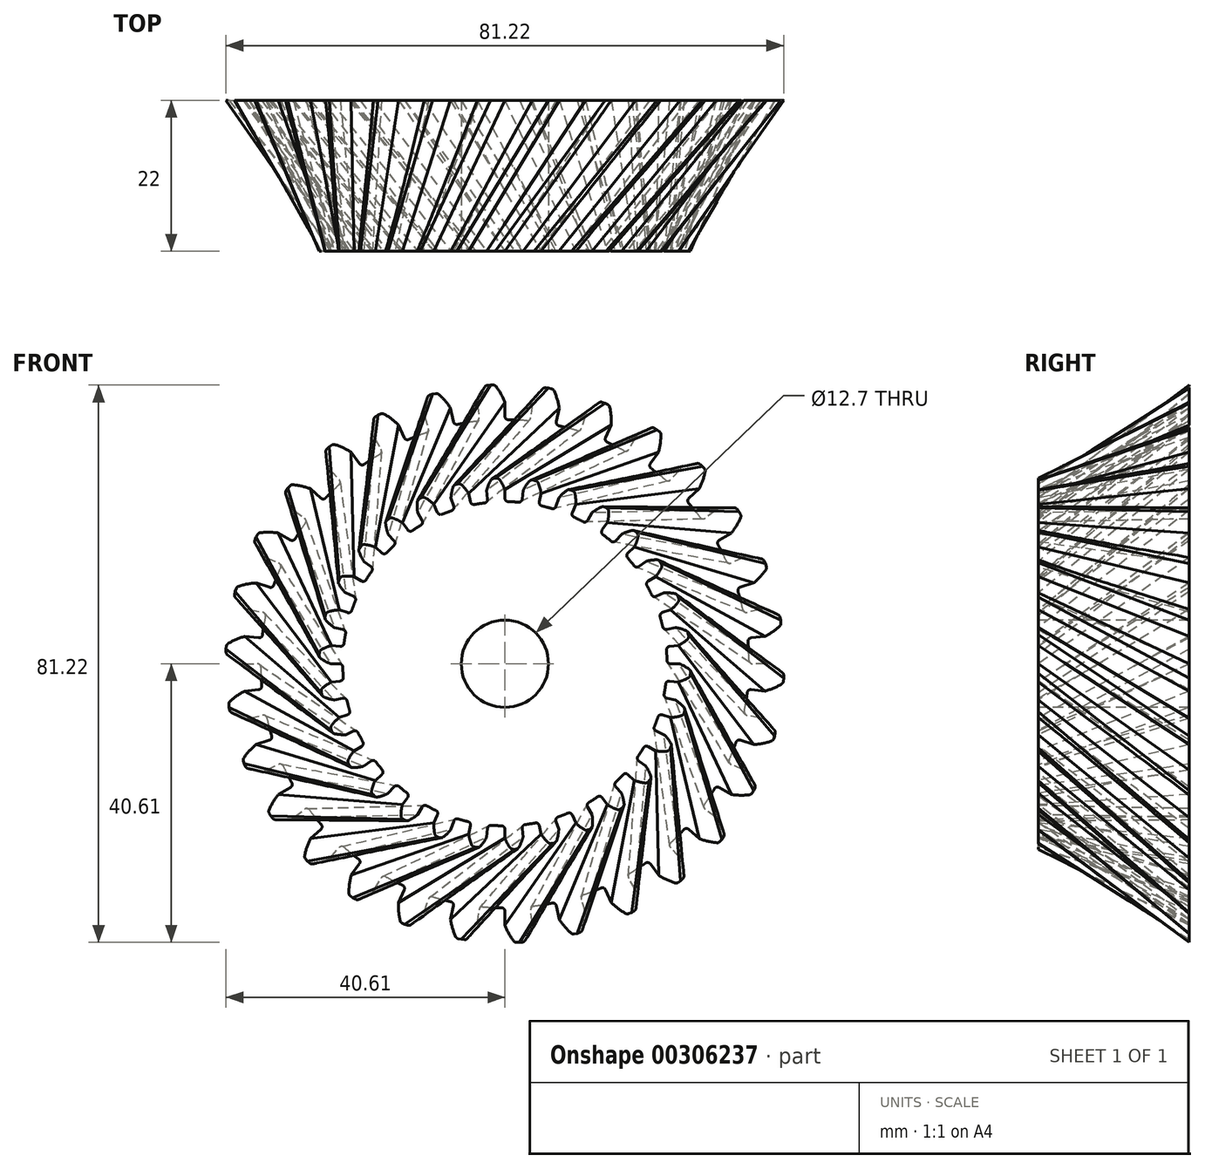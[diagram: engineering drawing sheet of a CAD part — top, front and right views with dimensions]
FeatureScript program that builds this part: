
annotation { "Feature Type Name" : "Feature", "Feature Type Description" : "" }
export const myFeature = defineFeature(function(context is Context, id is Id, definition is map)
    precondition{}
    {
        {
            var Q0;
            Q0=qCreatedBy(makeId("Front.planeOp"),FACE);
            var sketch = newSketch(context, id + "F0", { "sketchPlane" : qUnion([Q0])});
            skArc(sketch, "E0", {"start": v(-4.21, 35.3) * mm, "mid": v(-5.56, 35.12) * mm, "end": v(-6.9, 34.88) * mm});
            skLineSegment(sketch, "E1", {"start": v(0, 0) * mm, "end": v(-3.14, 59.92) * mm, "construction": true});
            skLineSegment(sketch, "E2", {"start": v(-1.69, 40.61) * mm, "end": v(-2.13, 40.61) * mm});
            skLineSegment(sketch, "E3", {"start": v(0, 38.1) * mm, "end": v(0, 36.06) * mm});
            skArc(sketch, "E4.trimOffspring", {"start": v(0, 38.1) * mm, "mid": v(-0.56, 39.3) * mm, "end": v(-1.28, 40.41) * mm});
            skLineSegment(sketch, "E5.MirrorCS", {"start": v(-2.57, 40.57) * mm, "end": v(-2.13, 40.61) * mm});
            skArc(sketch, "E6.MirrorCS", {"start": v(-3.98, 37.9) * mm, "mid": v(-3.55, 39.14) * mm, "end": v(-2.95, 40.32) * mm});
            skLineSegment(sketch, "E7.MirrorCS", {"start": v(-3.98, 37.9) * mm, "end": v(-3.77, 35.87) * mm});
            skPoint(sketch, "E8.visualSharp", {"position": v(-2.81, 40.54) * mm});
            skArc(sketch, "E8.filletArc", {"start": v(-2.57, 40.57) * mm, "mid": v(-2.79, 40.5) * mm, "end": v(-2.95, 40.32) * mm});
            skPoint(sketch, "E9.visualSharp", {"position": v(-1.44, 40.61) * mm});
            skArc(sketch, "E9.filletArc", {"start": v(-1.28, 40.41) * mm, "mid": v(-1.46, 40.56) * mm, "end": v(-1.69, 40.61) * mm});
            skPoint(sketch, "E10.orphan", {"position": v(-3.6, 34.32) * mm});
            skPoint(sketch, "E11.orphan", {"position": v(0, 34.5) * mm});
            skPoint(sketch, "E12.visualSharp", {"position": v(-3.72, 35.37) * mm});
            skArc(sketch, "E12.filletArc", {"start": v(-4.21, 35.3) * mm, "mid": v(-3.88, 35.5) * mm, "end": v(-3.77, 35.87) * mm});
            skPoint(sketch, "E13.visualSharp", {"position": v(0, 35.56) * mm});
            skArc(sketch, "E13.filletArc", {"start": v(0, 36.06) * mm, "mid": v(0.15, 35.7) * mm, "end": v(0.5, 35.56) * mm});
            skArc(sketch, "E14.1.0", {"start": v(-11.46, 33.66) * mm, "mid": v(-11.17, 33.91) * mm, "end": v(-11.14, 34.3) * mm});
            skLineSegment(sketch, "E14.1.1", {"start": v(-11.77, 36.24) * mm, "end": v(-11.14, 34.3) * mm});
            skArc(sketch, "E14.1.2", {"start": v(-11.77, 36.24) * mm, "mid": v(-11.61, 37.55) * mm, "end": v(-11.27, 38.83) * mm});
            skArc(sketch, "E14.1.3", {"start": v(-10.95, 39.15) * mm, "mid": v(-11.14, 39.03) * mm, "end": v(-11.27, 38.83) * mm});
            skLineSegment(sketch, "E14.1.4", {"start": v(-10.95, 39.15) * mm, "end": v(-10.53, 39.28) * mm});
            skLineSegment(sketch, "E14.1.5", {"start": v(-10.1, 39.38) * mm, "end": v(-10.53, 39.28) * mm});
            skArc(sketch, "E14.1.6", {"start": v(-9.66, 39.26) * mm, "mid": v(-9.86, 39.37) * mm, "end": v(-10.1, 39.38) * mm});
            skArc(sketch, "E14.1.7", {"start": v(-7.92, 37.27) * mm, "mid": v(-8.72, 38.33) * mm, "end": v(-9.66, 39.26) * mm});
            skLineSegment(sketch, "E14.1.8", {"start": v(-7.92, 37.27) * mm, "end": v(-7.5, 35.28) * mm});
            skArc(sketch, "E14.1.9", {"start": v(-7.5, 35.28) * mm, "mid": v(-7.28, 34.96) * mm, "end": v(-6.9, 34.88) * mm});
            skArc(sketch, "E14.2.0", {"start": v(-18.21, 30.54) * mm, "mid": v(-17.98, 30.85) * mm, "end": v(-18.03, 31.23) * mm});
            skLineSegment(sketch, "E14.2.1", {"start": v(-19.05, 33) * mm, "end": v(-18.03, 31.23) * mm});
            skArc(sketch, "E14.2.2", {"start": v(-19.05, 33) * mm, "mid": v(-19.16, 34.32) * mm, "end": v(-19.1, 35.64) * mm});
            skArc(sketch, "E14.2.3", {"start": v(-18.85, 36.02) * mm, "mid": v(-19.01, 35.86) * mm, "end": v(-19.1, 35.64) * mm});
            skLineSegment(sketch, "E14.2.4", {"start": v(-18.85, 36.02) * mm, "end": v(-18.46, 36.24) * mm});
            skLineSegment(sketch, "E14.2.5", {"start": v(-18.06, 36.42) * mm, "end": v(-18.46, 36.24) * mm});
            skArc(sketch, "E14.2.6", {"start": v(-17.6, 36.4) * mm, "mid": v(-17.83, 36.46) * mm, "end": v(-18.06, 36.42) * mm});
            skArc(sketch, "E14.2.7", {"start": v(-15.5, 34.8) * mm, "mid": v(-16.5, 35.68) * mm, "end": v(-17.6, 36.4) * mm});
            skLineSegment(sketch, "E14.2.8", {"start": v(-15.5, 34.8) * mm, "end": v(-14.67, 32.95) * mm});
            skArc(sketch, "E14.2.9", {"start": v(-14.67, 32.95) * mm, "mid": v(-14.4, 32.68) * mm, "end": v(-14, 32.69) * mm});
            skArc(sketch, "E14.3.0", {"start": v(-24.16, 26.09) * mm, "mid": v(-24, 26.44) * mm, "end": v(-24.13, 26.8) * mm});
            skLineSegment(sketch, "E14.3.1", {"start": v(-25.5, 28.31) * mm, "end": v(-24.13, 26.8) * mm});
            skArc(sketch, "E14.3.2", {"start": v(-25.5, 28.31) * mm, "mid": v(-25.88, 29.58) * mm, "end": v(-26.09, 30.9) * mm});
            skArc(sketch, "E14.3.3", {"start": v(-25.92, 31.31) * mm, "mid": v(-26.05, 31.12) * mm, "end": v(-26.09, 30.9) * mm});
            skLineSegment(sketch, "E14.3.4", {"start": v(-25.92, 31.31) * mm, "end": v(-25.6, 31.6) * mm});
            skLineSegment(sketch, "E14.3.5", {"start": v(-25.24, 31.87) * mm, "end": v(-25.6, 31.6) * mm});
            skArc(sketch, "E14.3.6", {"start": v(-24.8, 31.94) * mm, "mid": v(-25.02, 31.96) * mm, "end": v(-25.24, 31.87) * mm});
            skArc(sketch, "E14.3.7", {"start": v(-22.4, 30.82) * mm, "mid": v(-23.55, 31.47) * mm, "end": v(-24.8, 31.94) * mm});
            skLineSegment(sketch, "E14.3.8", {"start": v(-22.4, 30.82) * mm, "end": v(-21.2, 29.18) * mm});
            skArc(sketch, "E14.3.9", {"start": v(-21.2, 29.18) * mm, "mid": v(-20.87, 28.97) * mm, "end": v(-20.5, 29.06) * mm});
            skArc(sketch, "E14.4.0", {"start": v(-29.06, 20.5) * mm, "mid": v(-28.97, 20.87) * mm, "end": v(-29.18, 21.2) * mm});
            skLineSegment(sketch, "E14.4.1", {"start": v(-30.82, 22.4) * mm, "end": v(-29.18, 21.2) * mm});
            skArc(sketch, "E14.4.2", {"start": v(-30.82, 22.4) * mm, "mid": v(-31.47, 23.55) * mm, "end": v(-31.94, 24.8) * mm});
            skArc(sketch, "E14.4.3", {"start": v(-31.87, 25.24) * mm, "mid": v(-31.96, 25.02) * mm, "end": v(-31.94, 24.8) * mm});
            skLineSegment(sketch, "E14.4.4", {"start": v(-31.87, 25.24) * mm, "end": v(-31.6, 25.6) * mm});
            skLineSegment(sketch, "E14.4.5", {"start": v(-31.31, 25.92) * mm, "end": v(-31.6, 25.6) * mm});
            skArc(sketch, "E14.4.6", {"start": v(-30.9, 26.09) * mm, "mid": v(-31.12, 26.05) * mm, "end": v(-31.31, 25.92) * mm});
            skArc(sketch, "E14.4.7", {"start": v(-28.31, 25.5) * mm, "mid": v(-29.58, 25.88) * mm, "end": v(-30.9, 26.09) * mm});
            skLineSegment(sketch, "E14.4.8", {"start": v(-28.31, 25.5) * mm, "end": v(-26.8, 24.13) * mm});
            skArc(sketch, "E14.4.9", {"start": v(-26.8, 24.13) * mm, "mid": v(-26.44, 24) * mm, "end": v(-26.09, 24.16) * mm});
            skArc(sketch, "E14.5.0", {"start": v(-32.69, 14) * mm, "mid": v(-32.68, 14.4) * mm, "end": v(-32.95, 14.67) * mm});
            skLineSegment(sketch, "E14.5.1", {"start": v(-34.8, 15.5) * mm, "end": v(-32.95, 14.67) * mm});
            skArc(sketch, "E14.5.2", {"start": v(-34.8, 15.5) * mm, "mid": v(-35.68, 16.5) * mm, "end": v(-36.4, 17.6) * mm});
            skArc(sketch, "E14.5.3", {"start": v(-36.42, 18.06) * mm, "mid": v(-36.46, 17.83) * mm, "end": v(-36.4, 17.6) * mm});
            skLineSegment(sketch, "E14.5.4", {"start": v(-36.42, 18.06) * mm, "end": v(-36.24, 18.46) * mm});
            skLineSegment(sketch, "E14.5.5", {"start": v(-36.02, 18.85) * mm, "end": v(-36.24, 18.46) * mm});
            skArc(sketch, "E14.5.6", {"start": v(-35.64, 19.1) * mm, "mid": v(-35.86, 19.01) * mm, "end": v(-36.02, 18.85) * mm});
            skArc(sketch, "E14.5.7", {"start": v(-33, 19.05) * mm, "mid": v(-34.32, 19.16) * mm, "end": v(-35.64, 19.1) * mm});
            skLineSegment(sketch, "E14.5.8", {"start": v(-33, 19.05) * mm, "end": v(-31.23, 18.03) * mm});
            skArc(sketch, "E14.5.9", {"start": v(-31.23, 18.03) * mm, "mid": v(-30.85, 17.98) * mm, "end": v(-30.54, 18.21) * mm});
            skArc(sketch, "E14.6.0", {"start": v(-34.88, 6.9) * mm, "mid": v(-34.96, 7.28) * mm, "end": v(-35.28, 7.5) * mm});
            skLineSegment(sketch, "E14.6.1", {"start": v(-37.27, 7.92) * mm, "end": v(-35.28, 7.5) * mm});
            skArc(sketch, "E14.6.2", {"start": v(-37.27, 7.92) * mm, "mid": v(-38.33, 8.72) * mm, "end": v(-39.26, 9.66) * mm});
            skArc(sketch, "E14.6.3", {"start": v(-39.38, 10.1) * mm, "mid": v(-39.37, 9.86) * mm, "end": v(-39.26, 9.66) * mm});
            skLineSegment(sketch, "E14.6.4", {"start": v(-39.38, 10.1) * mm, "end": v(-39.28, 10.53) * mm});
            skLineSegment(sketch, "E14.6.5", {"start": v(-39.15, 10.95) * mm, "end": v(-39.28, 10.53) * mm});
            skArc(sketch, "E14.6.6", {"start": v(-38.83, 11.27) * mm, "mid": v(-39.03, 11.14) * mm, "end": v(-39.15, 10.95) * mm});
            skArc(sketch, "E14.6.7", {"start": v(-36.24, 11.77) * mm, "mid": v(-37.55, 11.61) * mm, "end": v(-38.83, 11.27) * mm});
            skLineSegment(sketch, "E14.6.8", {"start": v(-36.24, 11.77) * mm, "end": v(-34.3, 11.14) * mm});
            skArc(sketch, "E14.6.9", {"start": v(-34.3, 11.14) * mm, "mid": v(-33.91, 11.17) * mm, "end": v(-33.66, 11.46) * mm});
            skArc(sketch, "E14.7.0", {"start": v(-35.56, -0.5) * mm, "mid": v(-35.7, -0.15) * mm, "end": v(-36.06, 0) * mm});
            skLineSegment(sketch, "E14.7.1", {"start": v(-38.1, 0) * mm, "end": v(-36.06, 0) * mm});
            skArc(sketch, "E14.7.2", {"start": v(-38.1, 0) * mm, "mid": v(-39.3, 0.56) * mm, "end": v(-40.41, 1.28) * mm});
            skArc(sketch, "E14.7.3", {"start": v(-40.61, 1.69) * mm, "mid": v(-40.56, 1.46) * mm, "end": v(-40.41, 1.28) * mm});
            skLineSegment(sketch, "E14.7.4", {"start": v(-40.61, 1.69) * mm, "end": v(-40.61, 2.13) * mm});
            skLineSegment(sketch, "E14.7.5", {"start": v(-40.57, 2.57) * mm, "end": v(-40.61, 2.13) * mm});
            skArc(sketch, "E14.7.6", {"start": v(-40.32, 2.95) * mm, "mid": v(-40.5, 2.79) * mm, "end": v(-40.57, 2.57) * mm});
            skArc(sketch, "E14.7.7", {"start": v(-37.9, 3.98) * mm, "mid": v(-39.14, 3.55) * mm, "end": v(-40.32, 2.95) * mm});
            skLineSegment(sketch, "E14.7.8", {"start": v(-37.9, 3.98) * mm, "end": v(-35.87, 3.77) * mm});
            skArc(sketch, "E14.7.9", {"start": v(-35.87, 3.77) * mm, "mid": v(-35.5, 3.88) * mm, "end": v(-35.3, 4.21) * mm});
            skArc(sketch, "E14.8.0", {"start": v(-34.68, -7.88) * mm, "mid": v(-34.9, -7.57) * mm, "end": v(-35.28, -7.5) * mm});
            skLineSegment(sketch, "E14.8.1", {"start": v(-37.27, -7.92) * mm, "end": v(-35.28, -7.5) * mm});
            skArc(sketch, "E14.8.2", {"start": v(-37.27, -7.92) * mm, "mid": v(-38.56, -7.62) * mm, "end": v(-39.8, -7.15) * mm});
            skArc(sketch, "E14.8.3", {"start": v(-40.08, -6.8) * mm, "mid": v(-39.98, -7) * mm, "end": v(-39.8, -7.15) * mm});
            skLineSegment(sketch, "E14.8.4", {"start": v(-40.08, -6.8) * mm, "end": v(-40.17, -6.36) * mm});
            skLineSegment(sketch, "E14.8.5", {"start": v(-40.22, -5.92) * mm, "end": v(-40.17, -6.36) * mm});
            skArc(sketch, "E14.8.6", {"start": v(-40.06, -5.5) * mm, "mid": v(-40.19, -5.7) * mm, "end": v(-40.22, -5.92) * mm});
            skArc(sketch, "E14.8.7", {"start": v(-37.9, -3.98) * mm, "mid": v(-39.03, -4.67) * mm, "end": v(-40.06, -5.5) * mm});
            skLineSegment(sketch, "E14.8.8", {"start": v(-37.9, -3.98) * mm, "end": v(-35.87, -3.77) * mm});
            skArc(sketch, "E14.8.9", {"start": v(-35.87, -3.77) * mm, "mid": v(-35.53, -3.59) * mm, "end": v(-35.41, -3.22) * mm});
            skArc(sketch, "E14.9.0", {"start": v(-32.28, -14.92) * mm, "mid": v(-32.56, -14.66) * mm, "end": v(-32.95, -14.67) * mm});
            skLineSegment(sketch, "E14.9.1", {"start": v(-34.8, -15.5) * mm, "end": v(-32.95, -14.67) * mm});
            skArc(sketch, "E14.9.2", {"start": v(-34.8, -15.5) * mm, "mid": v(-36.13, -15.47) * mm, "end": v(-37.44, -15.27) * mm});
            skArc(sketch, "E14.9.3", {"start": v(-37.79, -14.98) * mm, "mid": v(-37.65, -15.16) * mm, "end": v(-37.44, -15.27) * mm});
            skLineSegment(sketch, "E14.9.4", {"start": v(-37.79, -14.98) * mm, "end": v(-37.97, -14.57) * mm});
            skLineSegment(sketch, "E14.9.5", {"start": v(-38.1, -14.16) * mm, "end": v(-37.97, -14.57) * mm});
            skArc(sketch, "E14.9.6", {"start": v(-38.04, -13.7) * mm, "mid": v(-38.12, -13.92) * mm, "end": v(-38.1, -14.16) * mm});
            skArc(sketch, "E14.9.7", {"start": v(-36.24, -11.77) * mm, "mid": v(-37.2, -12.68) * mm, "end": v(-38.04, -13.7) * mm});
            skLineSegment(sketch, "E14.9.8", {"start": v(-36.24, -11.77) * mm, "end": v(-34.3, -11.14) * mm});
            skArc(sketch, "E14.9.9", {"start": v(-34.3, -11.14) * mm, "mid": v(-34, -10.9) * mm, "end": v(-33.97, -10.51) * mm});
            skArc(sketch, "E14.10.0", {"start": v(-28.47, -21.3) * mm, "mid": v(-28.8, -21.1) * mm, "end": v(-29.18, -21.2) * mm});
            skLineSegment(sketch, "E14.10.1", {"start": v(-30.82, -22.4) * mm, "end": v(-29.18, -21.2) * mm});
            skArc(sketch, "E14.10.2", {"start": v(-30.82, -22.4) * mm, "mid": v(-32.12, -22.65) * mm, "end": v(-33.45, -22.72) * mm});
            skArc(sketch, "E14.10.3", {"start": v(-33.85, -22.5) * mm, "mid": v(-33.67, -22.66) * mm, "end": v(-33.45, -22.72) * mm});
            skLineSegment(sketch, "E14.10.4", {"start": v(-33.85, -22.5) * mm, "end": v(-34.1, -22.15) * mm});
            skLineSegment(sketch, "E14.10.5", {"start": v(-34.33, -21.77) * mm, "end": v(-34.1, -22.15) * mm});
            skArc(sketch, "E14.10.6", {"start": v(-34.36, -21.32) * mm, "mid": v(-34.4, -21.55) * mm, "end": v(-34.33, -21.77) * mm});
            skArc(sketch, "E14.10.7", {"start": v(-33, -19.05) * mm, "mid": v(-33.76, -20.14) * mm, "end": v(-34.36, -21.32) * mm});
            skLineSegment(sketch, "E14.10.8", {"start": v(-33, -19.05) * mm, "end": v(-31.23, -18.03) * mm});
            skArc(sketch, "E14.10.9", {"start": v(-31.23, -18.03) * mm, "mid": v(-31, -17.73) * mm, "end": v(-31.04, -17.34) * mm});
            skArc(sketch, "E14.11.0", {"start": v(-23.42, -26.76) * mm, "mid": v(-23.78, -26.63) * mm, "end": v(-24.13, -26.8) * mm});
            skLineSegment(sketch, "E14.11.1", {"start": v(-25.5, -28.31) * mm, "end": v(-24.13, -26.8) * mm});
            skArc(sketch, "E14.11.2", {"start": v(-25.5, -28.31) * mm, "mid": v(-26.71, -28.83) * mm, "end": v(-28, -29.17) * mm});
            skArc(sketch, "E14.11.3", {"start": v(-28.43, -29.05) * mm, "mid": v(-28.23, -29.16) * mm, "end": v(-28, -29.17) * mm});
            skLineSegment(sketch, "E14.11.4", {"start": v(-28.43, -29.05) * mm, "end": v(-28.76, -28.76) * mm});
            skLineSegment(sketch, "E14.11.5", {"start": v(-29.05, -28.43) * mm, "end": v(-28.76, -28.76) * mm});
            skArc(sketch, "E14.11.6", {"start": v(-29.17, -28) * mm, "mid": v(-29.16, -28.23) * mm, "end": v(-29.05, -28.43) * mm});
            skArc(sketch, "E14.11.7", {"start": v(-28.31, -25.5) * mm, "mid": v(-28.83, -26.71) * mm, "end": v(-29.17, -28) * mm});
            skLineSegment(sketch, "E14.11.8", {"start": v(-28.31, -25.5) * mm, "end": v(-26.8, -24.13) * mm});
            skArc(sketch, "E14.11.9", {"start": v(-26.8, -24.13) * mm, "mid": v(-26.63, -23.78) * mm, "end": v(-26.76, -23.42) * mm});
            skArc(sketch, "E14.12.0", {"start": v(-17.34, -31.04) * mm, "mid": v(-17.73, -31) * mm, "end": v(-18.03, -31.23) * mm});
            skLineSegment(sketch, "E14.12.1", {"start": v(-19.05, -33) * mm, "end": v(-18.03, -31.23) * mm});
            skArc(sketch, "E14.12.2", {"start": v(-19.05, -33) * mm, "mid": v(-20.14, -33.76) * mm, "end": v(-21.32, -34.36) * mm});
            skArc(sketch, "E14.12.3", {"start": v(-21.77, -34.33) * mm, "mid": v(-21.55, -34.4) * mm, "end": v(-21.32, -34.36) * mm});
            skLineSegment(sketch, "E14.12.4", {"start": v(-21.77, -34.33) * mm, "end": v(-22.15, -34.1) * mm});
            skLineSegment(sketch, "E14.12.5", {"start": v(-22.5, -33.85) * mm, "end": v(-22.15, -34.1) * mm});
            skArc(sketch, "E14.12.6", {"start": v(-22.72, -33.45) * mm, "mid": v(-22.66, -33.67) * mm, "end": v(-22.5, -33.85) * mm});
            skArc(sketch, "E14.12.7", {"start": v(-22.4, -30.82) * mm, "mid": v(-22.65, -32.12) * mm, "end": v(-22.72, -33.45) * mm});
            skLineSegment(sketch, "E14.12.8", {"start": v(-22.4, -30.82) * mm, "end": v(-21.2, -29.18) * mm});
            skArc(sketch, "E14.12.9", {"start": v(-21.2, -29.18) * mm, "mid": v(-21.1, -28.8) * mm, "end": v(-21.3, -28.47) * mm});
            skArc(sketch, "E14.13.0", {"start": v(-10.51, -33.97) * mm, "mid": v(-10.9, -34) * mm, "end": v(-11.14, -34.3) * mm});
            skLineSegment(sketch, "E14.13.1", {"start": v(-11.77, -36.24) * mm, "end": v(-11.14, -34.3) * mm});
            skArc(sketch, "E14.13.2", {"start": v(-11.77, -36.24) * mm, "mid": v(-12.68, -37.2) * mm, "end": v(-13.7, -38.04) * mm});
            skArc(sketch, "E14.13.3", {"start": v(-14.16, -38.1) * mm, "mid": v(-13.92, -38.12) * mm, "end": v(-13.7, -38.04) * mm});
            skLineSegment(sketch, "E14.13.4", {"start": v(-14.16, -38.1) * mm, "end": v(-14.57, -37.97) * mm});
            skLineSegment(sketch, "E14.13.5", {"start": v(-14.98, -37.79) * mm, "end": v(-14.57, -37.97) * mm});
            skArc(sketch, "E14.13.6", {"start": v(-15.27, -37.44) * mm, "mid": v(-15.16, -37.65) * mm, "end": v(-14.98, -37.79) * mm});
            skArc(sketch, "E14.13.7", {"start": v(-15.5, -34.8) * mm, "mid": v(-15.47, -36.13) * mm, "end": v(-15.27, -37.44) * mm});
            skLineSegment(sketch, "E14.13.8", {"start": v(-15.5, -34.8) * mm, "end": v(-14.67, -32.95) * mm});
            skArc(sketch, "E14.13.9", {"start": v(-14.67, -32.95) * mm, "mid": v(-14.66, -32.56) * mm, "end": v(-14.92, -32.28) * mm});
            skArc(sketch, "E14.14.0", {"start": v(-3.22, -35.41) * mm, "mid": v(-3.59, -35.53) * mm, "end": v(-3.77, -35.87) * mm});
            skLineSegment(sketch, "E14.14.1", {"start": v(-3.98, -37.9) * mm, "end": v(-3.77, -35.87) * mm});
            skArc(sketch, "E14.14.2", {"start": v(-3.98, -37.9) * mm, "mid": v(-4.67, -39.03) * mm, "end": v(-5.5, -40.06) * mm});
            skArc(sketch, "E14.14.3", {"start": v(-5.92, -40.22) * mm, "mid": v(-5.7, -40.19) * mm, "end": v(-5.5, -40.06) * mm});
            skLineSegment(sketch, "E14.14.4", {"start": v(-5.92, -40.22) * mm, "end": v(-6.36, -40.17) * mm});
            skLineSegment(sketch, "E14.14.5", {"start": v(-6.8, -40.08) * mm, "end": v(-6.36, -40.17) * mm});
            skArc(sketch, "E14.14.6", {"start": v(-7.15, -39.8) * mm, "mid": v(-7, -39.98) * mm, "end": v(-6.8, -40.08) * mm});
            skArc(sketch, "E14.14.7", {"start": v(-7.92, -37.27) * mm, "mid": v(-7.62, -38.56) * mm, "end": v(-7.15, -39.8) * mm});
            skLineSegment(sketch, "E14.14.8", {"start": v(-7.92, -37.27) * mm, "end": v(-7.5, -35.28) * mm});
            skArc(sketch, "E14.14.9", {"start": v(-7.5, -35.28) * mm, "mid": v(-7.57, -34.9) * mm, "end": v(-7.88, -34.68) * mm});
            skArc(sketch, "E14.15.0", {"start": v(4.21, -35.3) * mm, "mid": v(3.88, -35.5) * mm, "end": v(3.77, -35.87) * mm});
            skLineSegment(sketch, "E14.15.1", {"start": v(3.98, -37.9) * mm, "end": v(3.77, -35.87) * mm});
            skArc(sketch, "E14.15.2", {"start": v(3.98, -37.9) * mm, "mid": v(3.55, -39.14) * mm, "end": v(2.95, -40.32) * mm});
            skArc(sketch, "E14.15.3", {"start": v(2.57, -40.57) * mm, "mid": v(2.79, -40.5) * mm, "end": v(2.95, -40.32) * mm});
            skLineSegment(sketch, "E14.15.4", {"start": v(2.57, -40.57) * mm, "end": v(2.13, -40.61) * mm});
            skLineSegment(sketch, "E14.15.5", {"start": v(1.69, -40.61) * mm, "end": v(2.13, -40.61) * mm});
            skArc(sketch, "E14.15.6", {"start": v(1.28, -40.41) * mm, "mid": v(1.46, -40.56) * mm, "end": v(1.69, -40.61) * mm});
            skArc(sketch, "E14.15.7", {"start": v(0, -38.1) * mm, "mid": v(0.56, -39.3) * mm, "end": v(1.28, -40.41) * mm});
            skLineSegment(sketch, "E14.15.8", {"start": v(0, -38.1) * mm, "end": v(0, -36.06) * mm});
            skArc(sketch, "E14.15.9", {"start": v(0, -36.06) * mm, "mid": v(-0.15, -35.7) * mm, "end": v(-0.5, -35.56) * mm});
            skArc(sketch, "E14.16.0", {"start": v(11.46, -33.66) * mm, "mid": v(11.17, -33.91) * mm, "end": v(11.14, -34.3) * mm});
            skLineSegment(sketch, "E14.16.1", {"start": v(11.77, -36.24) * mm, "end": v(11.14, -34.3) * mm});
            skArc(sketch, "E14.16.2", {"start": v(11.77, -36.24) * mm, "mid": v(11.61, -37.55) * mm, "end": v(11.27, -38.83) * mm});
            skArc(sketch, "E14.16.3", {"start": v(10.95, -39.15) * mm, "mid": v(11.14, -39.03) * mm, "end": v(11.27, -38.83) * mm});
            skLineSegment(sketch, "E14.16.4", {"start": v(10.95, -39.15) * mm, "end": v(10.53, -39.28) * mm});
            skLineSegment(sketch, "E14.16.5", {"start": v(10.1, -39.38) * mm, "end": v(10.53, -39.28) * mm});
            skArc(sketch, "E14.16.6", {"start": v(9.66, -39.26) * mm, "mid": v(9.86, -39.37) * mm, "end": v(10.1, -39.38) * mm});
            skArc(sketch, "E14.16.7", {"start": v(7.92, -37.27) * mm, "mid": v(8.72, -38.33) * mm, "end": v(9.66, -39.26) * mm});
            skLineSegment(sketch, "E14.16.8", {"start": v(7.92, -37.27) * mm, "end": v(7.5, -35.28) * mm});
            skArc(sketch, "E14.16.9", {"start": v(7.5, -35.28) * mm, "mid": v(7.28, -34.96) * mm, "end": v(6.9, -34.88) * mm});
            skArc(sketch, "E14.17.0", {"start": v(18.21, -30.54) * mm, "mid": v(17.98, -30.85) * mm, "end": v(18.03, -31.23) * mm});
            skLineSegment(sketch, "E14.17.1", {"start": v(19.05, -33) * mm, "end": v(18.03, -31.23) * mm});
            skArc(sketch, "E14.17.2", {"start": v(19.05, -33) * mm, "mid": v(19.16, -34.32) * mm, "end": v(19.1, -35.64) * mm});
            skArc(sketch, "E14.17.3", {"start": v(18.85, -36.02) * mm, "mid": v(19.01, -35.86) * mm, "end": v(19.1, -35.64) * mm});
            skLineSegment(sketch, "E14.17.4", {"start": v(18.85, -36.02) * mm, "end": v(18.46, -36.24) * mm});
            skLineSegment(sketch, "E14.17.5", {"start": v(18.06, -36.42) * mm, "end": v(18.46, -36.24) * mm});
            skArc(sketch, "E14.17.6", {"start": v(17.6, -36.4) * mm, "mid": v(17.83, -36.46) * mm, "end": v(18.06, -36.42) * mm});
            skArc(sketch, "E14.17.7", {"start": v(15.5, -34.8) * mm, "mid": v(16.5, -35.68) * mm, "end": v(17.6, -36.4) * mm});
            skLineSegment(sketch, "E14.17.8", {"start": v(15.5, -34.8) * mm, "end": v(14.67, -32.95) * mm});
            skArc(sketch, "E14.17.9", {"start": v(14.67, -32.95) * mm, "mid": v(14.4, -32.68) * mm, "end": v(14, -32.69) * mm});
            skArc(sketch, "E14.18.0", {"start": v(24.16, -26.09) * mm, "mid": v(24, -26.44) * mm, "end": v(24.13, -26.8) * mm});
            skLineSegment(sketch, "E14.18.1", {"start": v(25.5, -28.31) * mm, "end": v(24.13, -26.8) * mm});
            skArc(sketch, "E14.18.2", {"start": v(25.5, -28.31) * mm, "mid": v(25.88, -29.58) * mm, "end": v(26.09, -30.9) * mm});
            skArc(sketch, "E14.18.3", {"start": v(25.92, -31.31) * mm, "mid": v(26.05, -31.12) * mm, "end": v(26.09, -30.9) * mm});
            skLineSegment(sketch, "E14.18.4", {"start": v(25.92, -31.31) * mm, "end": v(25.6, -31.6) * mm});
            skLineSegment(sketch, "E14.18.5", {"start": v(25.24, -31.87) * mm, "end": v(25.6, -31.6) * mm});
            skArc(sketch, "E14.18.6", {"start": v(24.8, -31.94) * mm, "mid": v(25.02, -31.96) * mm, "end": v(25.24, -31.87) * mm});
            skArc(sketch, "E14.18.7", {"start": v(22.4, -30.82) * mm, "mid": v(23.55, -31.47) * mm, "end": v(24.8, -31.94) * mm});
            skLineSegment(sketch, "E14.18.8", {"start": v(22.4, -30.82) * mm, "end": v(21.2, -29.18) * mm});
            skArc(sketch, "E14.18.9", {"start": v(21.2, -29.18) * mm, "mid": v(20.87, -28.97) * mm, "end": v(20.5, -29.06) * mm});
            skArc(sketch, "E14.19.0", {"start": v(29.06, -20.5) * mm, "mid": v(28.97, -20.87) * mm, "end": v(29.18, -21.2) * mm});
            skLineSegment(sketch, "E14.19.1", {"start": v(30.82, -22.4) * mm, "end": v(29.18, -21.2) * mm});
            skArc(sketch, "E14.19.2", {"start": v(30.82, -22.4) * mm, "mid": v(31.47, -23.55) * mm, "end": v(31.94, -24.8) * mm});
            skArc(sketch, "E14.19.3", {"start": v(31.87, -25.24) * mm, "mid": v(31.96, -25.02) * mm, "end": v(31.94, -24.8) * mm});
            skLineSegment(sketch, "E14.19.4", {"start": v(31.87, -25.24) * mm, "end": v(31.6, -25.6) * mm});
            skLineSegment(sketch, "E14.19.5", {"start": v(31.31, -25.92) * mm, "end": v(31.6, -25.6) * mm});
            skArc(sketch, "E14.19.6", {"start": v(30.9, -26.09) * mm, "mid": v(31.12, -26.05) * mm, "end": v(31.31, -25.92) * mm});
            skArc(sketch, "E14.19.7", {"start": v(28.31, -25.5) * mm, "mid": v(29.58, -25.88) * mm, "end": v(30.9, -26.09) * mm});
            skLineSegment(sketch, "E14.19.8", {"start": v(28.31, -25.5) * mm, "end": v(26.8, -24.13) * mm});
            skArc(sketch, "E14.19.9", {"start": v(26.8, -24.13) * mm, "mid": v(26.44, -24) * mm, "end": v(26.09, -24.16) * mm});
            skArc(sketch, "E14.20.0", {"start": v(32.69, -14) * mm, "mid": v(32.68, -14.4) * mm, "end": v(32.95, -14.67) * mm});
            skLineSegment(sketch, "E14.20.1", {"start": v(34.8, -15.5) * mm, "end": v(32.95, -14.67) * mm});
            skArc(sketch, "E14.20.2", {"start": v(34.8, -15.5) * mm, "mid": v(35.68, -16.5) * mm, "end": v(36.4, -17.6) * mm});
            skArc(sketch, "E14.20.3", {"start": v(36.42, -18.06) * mm, "mid": v(36.46, -17.83) * mm, "end": v(36.4, -17.6) * mm});
            skLineSegment(sketch, "E14.20.4", {"start": v(36.42, -18.06) * mm, "end": v(36.24, -18.46) * mm});
            skLineSegment(sketch, "E14.20.5", {"start": v(36.02, -18.85) * mm, "end": v(36.24, -18.46) * mm});
            skArc(sketch, "E14.20.6", {"start": v(35.64, -19.1) * mm, "mid": v(35.86, -19.01) * mm, "end": v(36.02, -18.85) * mm});
            skArc(sketch, "E14.20.7", {"start": v(33, -19.05) * mm, "mid": v(34.32, -19.16) * mm, "end": v(35.64, -19.1) * mm});
            skLineSegment(sketch, "E14.20.8", {"start": v(33, -19.05) * mm, "end": v(31.23, -18.03) * mm});
            skArc(sketch, "E14.20.9", {"start": v(31.23, -18.03) * mm, "mid": v(30.85, -17.98) * mm, "end": v(30.54, -18.21) * mm});
            skArc(sketch, "E14.21.0", {"start": v(34.88, -6.9) * mm, "mid": v(34.96, -7.28) * mm, "end": v(35.28, -7.5) * mm});
            skLineSegment(sketch, "E14.21.1", {"start": v(37.27, -7.92) * mm, "end": v(35.28, -7.5) * mm});
            skArc(sketch, "E14.21.2", {"start": v(37.27, -7.92) * mm, "mid": v(38.33, -8.72) * mm, "end": v(39.26, -9.66) * mm});
            skArc(sketch, "E14.21.3", {"start": v(39.38, -10.1) * mm, "mid": v(39.37, -9.86) * mm, "end": v(39.26, -9.66) * mm});
            skLineSegment(sketch, "E14.21.4", {"start": v(39.38, -10.1) * mm, "end": v(39.28, -10.53) * mm});
            skLineSegment(sketch, "E14.21.5", {"start": v(39.15, -10.95) * mm, "end": v(39.28, -10.53) * mm});
            skArc(sketch, "E14.21.6", {"start": v(38.83, -11.27) * mm, "mid": v(39.03, -11.14) * mm, "end": v(39.15, -10.95) * mm});
            skArc(sketch, "E14.21.7", {"start": v(36.24, -11.77) * mm, "mid": v(37.55, -11.61) * mm, "end": v(38.83, -11.27) * mm});
            skLineSegment(sketch, "E14.21.8", {"start": v(36.24, -11.77) * mm, "end": v(34.3, -11.14) * mm});
            skArc(sketch, "E14.21.9", {"start": v(34.3, -11.14) * mm, "mid": v(33.91, -11.17) * mm, "end": v(33.66, -11.46) * mm});
            skArc(sketch, "E14.22.0", {"start": v(35.56, 0.5) * mm, "mid": v(35.7, 0.15) * mm, "end": v(36.06, 0) * mm});
            skLineSegment(sketch, "E14.22.1", {"start": v(38.1, 0) * mm, "end": v(36.06, 0) * mm});
            skArc(sketch, "E14.22.2", {"start": v(38.1, 0) * mm, "mid": v(39.3, -0.56) * mm, "end": v(40.41, -1.28) * mm});
            skArc(sketch, "E14.22.3", {"start": v(40.61, -1.69) * mm, "mid": v(40.56, -1.46) * mm, "end": v(40.41, -1.28) * mm});
            skLineSegment(sketch, "E14.22.4", {"start": v(40.61, -1.69) * mm, "end": v(40.61, -2.13) * mm});
            skLineSegment(sketch, "E14.22.5", {"start": v(40.57, -2.57) * mm, "end": v(40.61, -2.13) * mm});
            skArc(sketch, "E14.22.6", {"start": v(40.32, -2.95) * mm, "mid": v(40.5, -2.79) * mm, "end": v(40.57, -2.57) * mm});
            skArc(sketch, "E14.22.7", {"start": v(37.9, -3.98) * mm, "mid": v(39.14, -3.55) * mm, "end": v(40.32, -2.95) * mm});
            skLineSegment(sketch, "E14.22.8", {"start": v(37.9, -3.98) * mm, "end": v(35.87, -3.77) * mm});
            skArc(sketch, "E14.22.9", {"start": v(35.87, -3.77) * mm, "mid": v(35.5, -3.88) * mm, "end": v(35.3, -4.21) * mm});
            skArc(sketch, "E14.23.0", {"start": v(34.68, 7.88) * mm, "mid": v(34.9, 7.57) * mm, "end": v(35.28, 7.5) * mm});
            skLineSegment(sketch, "E14.23.1", {"start": v(37.27, 7.92) * mm, "end": v(35.28, 7.5) * mm});
            skArc(sketch, "E14.23.2", {"start": v(37.27, 7.92) * mm, "mid": v(38.56, 7.62) * mm, "end": v(39.8, 7.15) * mm});
            skArc(sketch, "E14.23.3", {"start": v(40.08, 6.8) * mm, "mid": v(39.98, 7) * mm, "end": v(39.8, 7.15) * mm});
            skLineSegment(sketch, "E14.23.4", {"start": v(40.08, 6.8) * mm, "end": v(40.17, 6.36) * mm});
            skLineSegment(sketch, "E14.23.5", {"start": v(40.22, 5.92) * mm, "end": v(40.17, 6.36) * mm});
            skArc(sketch, "E14.23.6", {"start": v(40.06, 5.5) * mm, "mid": v(40.19, 5.7) * mm, "end": v(40.22, 5.92) * mm});
            skArc(sketch, "E14.23.7", {"start": v(37.9, 3.98) * mm, "mid": v(39.03, 4.67) * mm, "end": v(40.06, 5.5) * mm});
            skLineSegment(sketch, "E14.23.8", {"start": v(37.9, 3.98) * mm, "end": v(35.87, 3.77) * mm});
            skArc(sketch, "E14.23.9", {"start": v(35.87, 3.77) * mm, "mid": v(35.53, 3.59) * mm, "end": v(35.41, 3.22) * mm});
            skArc(sketch, "E14.24.0", {"start": v(32.28, 14.92) * mm, "mid": v(32.56, 14.66) * mm, "end": v(32.95, 14.67) * mm});
            skLineSegment(sketch, "E14.24.1", {"start": v(34.8, 15.5) * mm, "end": v(32.95, 14.67) * mm});
            skArc(sketch, "E14.24.2", {"start": v(34.8, 15.5) * mm, "mid": v(36.13, 15.47) * mm, "end": v(37.44, 15.27) * mm});
            skArc(sketch, "E14.24.3", {"start": v(37.79, 14.98) * mm, "mid": v(37.65, 15.16) * mm, "end": v(37.44, 15.27) * mm});
            skLineSegment(sketch, "E14.24.4", {"start": v(37.79, 14.98) * mm, "end": v(37.97, 14.57) * mm});
            skLineSegment(sketch, "E14.24.5", {"start": v(38.1, 14.16) * mm, "end": v(37.97, 14.57) * mm});
            skArc(sketch, "E14.24.6", {"start": v(38.04, 13.7) * mm, "mid": v(38.12, 13.92) * mm, "end": v(38.1, 14.16) * mm});
            skArc(sketch, "E14.24.7", {"start": v(36.24, 11.77) * mm, "mid": v(37.2, 12.68) * mm, "end": v(38.04, 13.7) * mm});
            skLineSegment(sketch, "E14.24.8", {"start": v(36.24, 11.77) * mm, "end": v(34.3, 11.14) * mm});
            skArc(sketch, "E14.24.9", {"start": v(34.3, 11.14) * mm, "mid": v(34, 10.9) * mm, "end": v(33.97, 10.51) * mm});
            skArc(sketch, "E14.25.0", {"start": v(28.47, 21.3) * mm, "mid": v(28.8, 21.1) * mm, "end": v(29.18, 21.2) * mm});
            skLineSegment(sketch, "E14.25.1", {"start": v(30.82, 22.4) * mm, "end": v(29.18, 21.2) * mm});
            skArc(sketch, "E14.25.2", {"start": v(30.82, 22.4) * mm, "mid": v(32.12, 22.65) * mm, "end": v(33.45, 22.72) * mm});
            skArc(sketch, "E14.25.3", {"start": v(33.85, 22.5) * mm, "mid": v(33.67, 22.66) * mm, "end": v(33.45, 22.72) * mm});
            skLineSegment(sketch, "E14.25.4", {"start": v(33.85, 22.5) * mm, "end": v(34.1, 22.15) * mm});
            skLineSegment(sketch, "E14.25.5", {"start": v(34.33, 21.77) * mm, "end": v(34.1, 22.15) * mm});
            skArc(sketch, "E14.25.6", {"start": v(34.36, 21.32) * mm, "mid": v(34.4, 21.55) * mm, "end": v(34.33, 21.77) * mm});
            skArc(sketch, "E14.25.7", {"start": v(33, 19.05) * mm, "mid": v(33.76, 20.14) * mm, "end": v(34.36, 21.32) * mm});
            skLineSegment(sketch, "E14.25.8", {"start": v(33, 19.05) * mm, "end": v(31.23, 18.03) * mm});
            skArc(sketch, "E14.25.9", {"start": v(31.23, 18.03) * mm, "mid": v(31, 17.73) * mm, "end": v(31.04, 17.34) * mm});
            skArc(sketch, "E14.26.0", {"start": v(23.42, 26.76) * mm, "mid": v(23.78, 26.63) * mm, "end": v(24.13, 26.8) * mm});
            skLineSegment(sketch, "E14.26.1", {"start": v(25.5, 28.31) * mm, "end": v(24.13, 26.8) * mm});
            skArc(sketch, "E14.26.2", {"start": v(25.5, 28.31) * mm, "mid": v(26.71, 28.83) * mm, "end": v(28, 29.17) * mm});
            skArc(sketch, "E14.26.3", {"start": v(28.43, 29.05) * mm, "mid": v(28.23, 29.16) * mm, "end": v(28, 29.17) * mm});
            skLineSegment(sketch, "E14.26.4", {"start": v(28.43, 29.05) * mm, "end": v(28.76, 28.76) * mm});
            skLineSegment(sketch, "E14.26.5", {"start": v(29.05, 28.43) * mm, "end": v(28.76, 28.76) * mm});
            skArc(sketch, "E14.26.6", {"start": v(29.17, 28) * mm, "mid": v(29.16, 28.23) * mm, "end": v(29.05, 28.43) * mm});
            skArc(sketch, "E14.26.7", {"start": v(28.31, 25.5) * mm, "mid": v(28.83, 26.71) * mm, "end": v(29.17, 28) * mm});
            skLineSegment(sketch, "E14.26.8", {"start": v(28.31, 25.5) * mm, "end": v(26.8, 24.13) * mm});
            skArc(sketch, "E14.26.9", {"start": v(26.8, 24.13) * mm, "mid": v(26.63, 23.78) * mm, "end": v(26.76, 23.42) * mm});
            skArc(sketch, "E14.27.0", {"start": v(17.34, 31.04) * mm, "mid": v(17.73, 31) * mm, "end": v(18.03, 31.23) * mm});
            skLineSegment(sketch, "E14.27.1", {"start": v(19.05, 33) * mm, "end": v(18.03, 31.23) * mm});
            skArc(sketch, "E14.27.2", {"start": v(19.05, 33) * mm, "mid": v(20.14, 33.76) * mm, "end": v(21.32, 34.36) * mm});
            skArc(sketch, "E14.27.3", {"start": v(21.77, 34.33) * mm, "mid": v(21.55, 34.4) * mm, "end": v(21.32, 34.36) * mm});
            skLineSegment(sketch, "E14.27.4", {"start": v(21.77, 34.33) * mm, "end": v(22.15, 34.1) * mm});
            skLineSegment(sketch, "E14.27.5", {"start": v(22.5, 33.85) * mm, "end": v(22.15, 34.1) * mm});
            skArc(sketch, "E14.27.6", {"start": v(22.72, 33.45) * mm, "mid": v(22.66, 33.67) * mm, "end": v(22.5, 33.85) * mm});
            skArc(sketch, "E14.27.7", {"start": v(22.4, 30.82) * mm, "mid": v(22.65, 32.12) * mm, "end": v(22.72, 33.45) * mm});
            skLineSegment(sketch, "E14.27.8", {"start": v(22.4, 30.82) * mm, "end": v(21.2, 29.18) * mm});
            skArc(sketch, "E14.27.9", {"start": v(21.2, 29.18) * mm, "mid": v(21.1, 28.8) * mm, "end": v(21.3, 28.47) * mm});
            skArc(sketch, "E14.28.0", {"start": v(10.51, 33.97) * mm, "mid": v(10.9, 34) * mm, "end": v(11.14, 34.3) * mm});
            skLineSegment(sketch, "E14.28.1", {"start": v(11.77, 36.24) * mm, "end": v(11.14, 34.3) * mm});
            skArc(sketch, "E14.28.2", {"start": v(11.77, 36.24) * mm, "mid": v(12.68, 37.2) * mm, "end": v(13.7, 38.04) * mm});
            skArc(sketch, "E14.28.3", {"start": v(14.16, 38.1) * mm, "mid": v(13.92, 38.12) * mm, "end": v(13.7, 38.04) * mm});
            skLineSegment(sketch, "E14.28.4", {"start": v(14.16, 38.1) * mm, "end": v(14.57, 37.97) * mm});
            skLineSegment(sketch, "E14.28.5", {"start": v(14.98, 37.79) * mm, "end": v(14.57, 37.97) * mm});
            skArc(sketch, "E14.28.6", {"start": v(15.27, 37.44) * mm, "mid": v(15.16, 37.65) * mm, "end": v(14.98, 37.79) * mm});
            skArc(sketch, "E14.28.7", {"start": v(15.5, 34.8) * mm, "mid": v(15.47, 36.13) * mm, "end": v(15.27, 37.44) * mm});
            skLineSegment(sketch, "E14.28.8", {"start": v(15.5, 34.8) * mm, "end": v(14.67, 32.95) * mm});
            skArc(sketch, "E14.28.9", {"start": v(14.67, 32.95) * mm, "mid": v(14.66, 32.56) * mm, "end": v(14.92, 32.28) * mm});
            skArc(sketch, "E14.29.0", {"start": v(3.22, 35.41) * mm, "mid": v(3.59, 35.53) * mm, "end": v(3.77, 35.87) * mm});
            skLineSegment(sketch, "E14.29.1", {"start": v(3.98, 37.9) * mm, "end": v(3.77, 35.87) * mm});
            skArc(sketch, "E14.29.2", {"start": v(3.98, 37.9) * mm, "mid": v(4.67, 39.03) * mm, "end": v(5.5, 40.06) * mm});
            skArc(sketch, "E14.29.3", {"start": v(5.92, 40.22) * mm, "mid": v(5.7, 40.19) * mm, "end": v(5.5, 40.06) * mm});
            skLineSegment(sketch, "E14.29.4", {"start": v(5.92, 40.22) * mm, "end": v(6.36, 40.17) * mm});
            skLineSegment(sketch, "E14.29.5", {"start": v(6.8, 40.08) * mm, "end": v(6.36, 40.17) * mm});
            skArc(sketch, "E14.29.6", {"start": v(7.15, 39.8) * mm, "mid": v(7, 39.98) * mm, "end": v(6.8, 40.08) * mm});
            skArc(sketch, "E14.29.7", {"start": v(7.92, 37.27) * mm, "mid": v(7.62, 38.56) * mm, "end": v(7.15, 39.8) * mm});
            skLineSegment(sketch, "E14.29.8", {"start": v(7.92, 37.27) * mm, "end": v(7.5, 35.28) * mm});
            skArc(sketch, "E14.29.9", {"start": v(7.5, 35.28) * mm, "mid": v(7.57, 34.9) * mm, "end": v(7.88, 34.68) * mm});
            skArc(sketch, "E15.trimOffspring", {"start": v(-11.46, 33.66) * mm, "mid": v(-12.74, 33.2) * mm, "end": v(-14, 32.69) * mm});
            skArc(sketch, "E16.trimOffspring", {"start": v(-18.21, 30.54) * mm, "mid": v(-19.37, 29.82) * mm, "end": v(-20.5, 29.06) * mm});
            skArc(sketch, "E17.trimOffspring", {"start": v(-24.16, 26.09) * mm, "mid": v(-25.14, 25.14) * mm, "end": v(-26.09, 24.16) * mm});
            skArc(sketch, "E18.trimOffspring", {"start": v(-29.06, 20.5) * mm, "mid": v(-29.82, 19.37) * mm, "end": v(-30.54, 18.21) * mm});
            skArc(sketch, "E19.trimOffspring", {"start": v(-32.69, 14) * mm, "mid": v(-33.2, 12.74) * mm, "end": v(-33.66, 11.46) * mm});
            skArc(sketch, "E20.trimOffspring", {"start": v(-34.88, 6.9) * mm, "mid": v(-35.12, 5.56) * mm, "end": v(-35.3, 4.21) * mm});
            skArc(sketch, "E21.trimOffspring", {"start": v(-35.56, -0.5) * mm, "mid": v(-35.51, -1.86) * mm, "end": v(-35.41, -3.22) * mm});
            skArc(sketch, "E22.trimOffspring", {"start": v(-34.68, -7.88) * mm, "mid": v(-34.35, -9.2) * mm, "end": v(-33.97, -10.51) * mm});
            skArc(sketch, "E23.trimOffspring", {"start": v(-32.28, -14.92) * mm, "mid": v(-31.68, -16.14) * mm, "end": v(-31.04, -17.34) * mm});
            skArc(sketch, "E24.trimOffspring", {"start": v(-28.47, -21.3) * mm, "mid": v(-27.64, -22.38) * mm, "end": v(-26.76, -23.42) * mm});
            skArc(sketch, "E25.trimOffspring", {"start": v(3.22, 35.41) * mm, "mid": v(1.86, 35.51) * mm, "end": v(0.5, 35.56) * mm});
            skArc(sketch, "E26.trimOffspring", {"start": v(10.51, 33.97) * mm, "mid": v(9.2, 34.35) * mm, "end": v(7.88, 34.68) * mm});
            skArc(sketch, "E27.trimOffspring", {"start": v(17.34, 31.04) * mm, "mid": v(16.14, 31.68) * mm, "end": v(14.92, 32.28) * mm});
            skArc(sketch, "E28.trimOffspring", {"start": v(23.42, 26.76) * mm, "mid": v(22.38, 27.64) * mm, "end": v(21.3, 28.47) * mm});
            skArc(sketch, "E29.trimOffspring", {"start": v(28.47, 21.3) * mm, "mid": v(27.64, 22.38) * mm, "end": v(26.76, 23.42) * mm});
            skArc(sketch, "E30.trimOffspring", {"start": v(32.28, 14.92) * mm, "mid": v(31.68, 16.14) * mm, "end": v(31.04, 17.34) * mm});
            skArc(sketch, "E31.trimOffspring", {"start": v(34.68, 7.88) * mm, "mid": v(34.35, 9.2) * mm, "end": v(33.97, 10.51) * mm});
            skArc(sketch, "E32.trimOffspring", {"start": v(35.56, 0.5) * mm, "mid": v(35.51, 1.86) * mm, "end": v(35.41, 3.22) * mm});
            skArc(sketch, "E33.trimOffspring", {"start": v(34.88, -6.9) * mm, "mid": v(35.12, -5.56) * mm, "end": v(35.3, -4.21) * mm});
            skArc(sketch, "E34.trimOffspring", {"start": v(32.69, -14) * mm, "mid": v(33.2, -12.74) * mm, "end": v(33.66, -11.46) * mm});
            skArc(sketch, "E35.trimOffspring", {"start": v(29.06, -20.5) * mm, "mid": v(29.82, -19.37) * mm, "end": v(30.54, -18.21) * mm});
            skArc(sketch, "E36.trimOffspring", {"start": v(24.16, -26.09) * mm, "mid": v(25.14, -25.14) * mm, "end": v(26.09, -24.16) * mm});
            skArc(sketch, "E37.trimOffspring", {"start": v(18.21, -30.54) * mm, "mid": v(19.37, -29.82) * mm, "end": v(20.5, -29.06) * mm});
            skArc(sketch, "E38.trimOffspring", {"start": v(11.46, -33.66) * mm, "mid": v(12.74, -33.2) * mm, "end": v(14, -32.69) * mm});
            skArc(sketch, "E39.trimOffspring", {"start": v(4.21, -35.3) * mm, "mid": v(5.56, -35.12) * mm, "end": v(6.9, -34.88) * mm});
            skArc(sketch, "E40.trimOffspring", {"start": v(-3.22, -35.41) * mm, "mid": v(-1.86, -35.51) * mm, "end": v(-0.5, -35.56) * mm});
            skArc(sketch, "E41.trimOffspring", {"start": v(-10.51, -33.97) * mm, "mid": v(-9.2, -34.35) * mm, "end": v(-7.88, -34.68) * mm});
            skArc(sketch, "E42.trimOffspring", {"start": v(-17.34, -31.04) * mm, "mid": v(-16.14, -31.68) * mm, "end": v(-14.92, -32.28) * mm});
            skArc(sketch, "E43.trimOffspring", {"start": v(-23.42, -26.76) * mm, "mid": v(-22.38, -27.64) * mm, "end": v(-21.3, -28.47) * mm});
            skSolve(sketch);
        }
        {
            var Q0;
            Q0=makeQuery(id+"F0.imprint","IMPRINT",FACE,{"disambiguationData":[TD([[makeQuery(id+"F0.imprint","IMPRINT",EDGE,{"derivedFrom":sQuery(id+"F0.wireOp",EDGE,"E0")}),1.0]])]});
            cPlane(context, id + "F1", {"entities" : qUnion([Q0]), "cplaneType" : CPlaneType.OFFSET, "offset" : 22 * mm, "width" : 152.4 * mm, "height" : 152.4 * mm});
        }
        {
            var Q0;
            Q0=qCreatedBy(id+"F1.planeOp",FACE);
            var sketch = newSketch(context, id + "F2", { "sketchPlane" : qUnion([Q0])});
            skArc(sketch, "E44", {"start": v(-2.96, 23.44) * mm, "mid": v(-3.7, 23.33) * mm, "end": v(-4.42, 23.2) * mm});
            skLineSegment(sketch, "E45", {"start": v(0, 0) * mm, "end": v(-2.34, 44.7) * mm, "construction": true});
            skLineSegment(sketch, "E46", {"start": v(-1.18, 27.04) * mm, "end": v(-1.42, 27.04) * mm});
            skLineSegment(sketch, "E47", {"start": v(0, 25.4) * mm, "end": v(0, 24.12) * mm});
            skArc(sketch, "E48.trimOffspring", {"start": v(0, 25.4) * mm, "mid": v(-0.34, 26.14) * mm, "end": v(-0.77, 26.82) * mm});
            skLineSegment(sketch, "E49.MirrorCS", {"start": v(-1.65, 27.01) * mm, "end": v(-1.42, 27.04) * mm});
            skArc(sketch, "E50.MirrorCS", {"start": v(-2.66, 25.26) * mm, "mid": v(-2.4, 26.03) * mm, "end": v(-2.04, 26.76) * mm});
            skLineSegment(sketch, "E51.MirrorCS", {"start": v(-2.66, 25.26) * mm, "end": v(-2.52, 24) * mm});
            skPoint(sketch, "E52.orphan", {"position": v(-2.08, 19.75) * mm});
            skPoint(sketch, "E53.orphan", {"position": v(0, 19.86) * mm});
            skPoint(sketch, "E54.visualSharp", {"position": v(-1.9, 26.98) * mm});
            skArc(sketch, "E54.filletArc", {"start": v(-1.65, 27.01) * mm, "mid": v(-1.88, 26.93) * mm, "end": v(-2.04, 26.76) * mm});
            skPoint(sketch, "E55.visualSharp", {"position": v(-0.93, 27.04) * mm});
            skArc(sketch, "E55.filletArc", {"start": v(-0.77, 26.82) * mm, "mid": v(-0.95, 26.98) * mm, "end": v(-1.18, 27.04) * mm});
            skPoint(sketch, "E56.visualSharp", {"position": v(0, 23.62) * mm});
            skArc(sketch, "E56.filletArc", {"start": v(0, 24.12) * mm, "mid": v(0.15, 23.77) * mm, "end": v(0.5, 23.62) * mm});
            skPoint(sketch, "E57.visualSharp", {"position": v(-2.47, 23.5) * mm});
            skArc(sketch, "E57.filletArc", {"start": v(-2.96, 23.44) * mm, "mid": v(-2.63, 23.62) * mm, "end": v(-2.52, 24) * mm});
            skArc(sketch, "E58.1.0", {"start": v(-7.77, 22.3) * mm, "mid": v(-7.48, 22.56) * mm, "end": v(-7.45, 22.94) * mm});
            skLineSegment(sketch, "E58.1.1", {"start": v(-7.85, 24.16) * mm, "end": v(-7.45, 22.94) * mm});
            skArc(sketch, "E58.1.2", {"start": v(-7.85, 24.16) * mm, "mid": v(-7.75, 24.96) * mm, "end": v(-7.56, 25.75) * mm});
            skArc(sketch, "E58.1.3", {"start": v(-7.23, 26.08) * mm, "mid": v(-7.43, 25.95) * mm, "end": v(-7.56, 25.75) * mm});
            skLineSegment(sketch, "E58.1.4", {"start": v(-7.23, 26.08) * mm, "end": v(-7, 26.15) * mm});
            skLineSegment(sketch, "E58.1.5", {"start": v(-6.78, 26.2) * mm, "end": v(-7, 26.15) * mm});
            skArc(sketch, "E58.1.6", {"start": v(-6.33, 26.08) * mm, "mid": v(-6.54, 26.2) * mm, "end": v(-6.78, 26.2) * mm});
            skArc(sketch, "E58.1.7", {"start": v(-5.28, 24.84) * mm, "mid": v(-5.77, 25.5) * mm, "end": v(-6.33, 26.08) * mm});
            skLineSegment(sketch, "E58.1.8", {"start": v(-5.28, 24.84) * mm, "end": v(-5.02, 23.6) * mm});
            skArc(sketch, "E58.1.9", {"start": v(-5.02, 23.6) * mm, "mid": v(-4.8, 23.28) * mm, "end": v(-4.42, 23.2) * mm});
            skArc(sketch, "E58.2.0", {"start": v(-12.24, 20.2) * mm, "mid": v(-12.01, 20.51) * mm, "end": v(-12.06, 20.9) * mm});
            skLineSegment(sketch, "E58.2.1", {"start": v(-12.7, 22) * mm, "end": v(-12.06, 20.9) * mm});
            skArc(sketch, "E58.2.2", {"start": v(-12.7, 22) * mm, "mid": v(-12.77, 22.8) * mm, "end": v(-12.75, 23.61) * mm});
            skArc(sketch, "E58.2.3", {"start": v(-12.5, 24) * mm, "mid": v(-12.67, 23.84) * mm, "end": v(-12.75, 23.61) * mm});
            skLineSegment(sketch, "E58.2.4", {"start": v(-12.5, 24) * mm, "end": v(-12.3, 24.12) * mm});
            skLineSegment(sketch, "E58.2.5", {"start": v(-12.07, 24.22) * mm, "end": v(-12.3, 24.12) * mm});
            skArc(sketch, "E58.2.6", {"start": v(-11.61, 24.2) * mm, "mid": v(-11.84, 24.26) * mm, "end": v(-12.07, 24.22) * mm});
            skArc(sketch, "E58.2.7", {"start": v(-10.33, 23.2) * mm, "mid": v(-10.94, 23.74) * mm, "end": v(-11.61, 24.2) * mm});
            skLineSegment(sketch, "E58.2.8", {"start": v(-10.33, 23.2) * mm, "end": v(-9.81, 22.04) * mm});
            skArc(sketch, "E58.2.9", {"start": v(-9.81, 22.04) * mm, "mid": v(-9.54, 21.77) * mm, "end": v(-9.15, 21.78) * mm});
            skArc(sketch, "E58.3.0", {"start": v(-16.17, 17.22) * mm, "mid": v(-16.01, 17.57) * mm, "end": v(-16.14, 17.93) * mm});
            skLineSegment(sketch, "E58.3.1", {"start": v(-17, 18.88) * mm, "end": v(-16.14, 17.93) * mm});
            skArc(sketch, "E58.3.2", {"start": v(-17, 18.88) * mm, "mid": v(-17.24, 19.65) * mm, "end": v(-17.38, 20.45) * mm});
            skArc(sketch, "E58.3.3", {"start": v(-17.21, 20.88) * mm, "mid": v(-17.35, 20.68) * mm, "end": v(-17.38, 20.45) * mm});
            skLineSegment(sketch, "E58.3.4", {"start": v(-17.21, 20.88) * mm, "end": v(-17.04, 21.04) * mm});
            skLineSegment(sketch, "E58.3.5", {"start": v(-16.85, 21.18) * mm, "end": v(-17.04, 21.04) * mm});
            skArc(sketch, "E58.3.6", {"start": v(-16.39, 21.25) * mm, "mid": v(-16.63, 21.27) * mm, "end": v(-16.85, 21.18) * mm});
            skArc(sketch, "E58.3.7", {"start": v(-14.93, 20.55) * mm, "mid": v(-15.64, 20.95) * mm, "end": v(-16.39, 21.25) * mm});
            skLineSegment(sketch, "E58.3.8", {"start": v(-14.93, 20.55) * mm, "end": v(-14.18, 19.52) * mm});
            skArc(sketch, "E58.3.9", {"start": v(-14.18, 19.52) * mm, "mid": v(-13.85, 19.31) * mm, "end": v(-13.48, 19.4) * mm});
            skArc(sketch, "E58.4.0", {"start": v(-19.4, 13.48) * mm, "mid": v(-19.31, 13.85) * mm, "end": v(-19.52, 14.18) * mm});
            skLineSegment(sketch, "E58.4.1", {"start": v(-20.55, 14.93) * mm, "end": v(-19.52, 14.18) * mm});
            skArc(sketch, "E58.4.2", {"start": v(-20.55, 14.93) * mm, "mid": v(-20.95, 15.64) * mm, "end": v(-21.25, 16.39) * mm});
            skArc(sketch, "E58.4.3", {"start": v(-21.18, 16.85) * mm, "mid": v(-21.27, 16.63) * mm, "end": v(-21.25, 16.39) * mm});
            skLineSegment(sketch, "E58.4.4", {"start": v(-21.18, 16.85) * mm, "end": v(-21.04, 17.04) * mm});
            skLineSegment(sketch, "E58.4.5", {"start": v(-20.88, 17.21) * mm, "end": v(-21.04, 17.04) * mm});
            skArc(sketch, "E58.4.6", {"start": v(-20.45, 17.38) * mm, "mid": v(-20.68, 17.35) * mm, "end": v(-20.88, 17.21) * mm});
            skArc(sketch, "E58.4.7", {"start": v(-18.88, 17) * mm, "mid": v(-19.65, 17.24) * mm, "end": v(-20.45, 17.38) * mm});
            skLineSegment(sketch, "E58.4.8", {"start": v(-18.88, 17) * mm, "end": v(-17.93, 16.14) * mm});
            skArc(sketch, "E58.4.9", {"start": v(-17.93, 16.14) * mm, "mid": v(-17.57, 16.01) * mm, "end": v(-17.22, 16.17) * mm});
            skArc(sketch, "E58.5.0", {"start": v(-21.78, 9.15) * mm, "mid": v(-21.77, 9.54) * mm, "end": v(-22.04, 9.81) * mm});
            skLineSegment(sketch, "E58.5.1", {"start": v(-23.2, 10.33) * mm, "end": v(-22.04, 9.81) * mm});
            skArc(sketch, "E58.5.2", {"start": v(-23.2, 10.33) * mm, "mid": v(-23.74, 10.94) * mm, "end": v(-24.2, 11.61) * mm});
            skArc(sketch, "E58.5.3", {"start": v(-24.22, 12.07) * mm, "mid": v(-24.26, 11.84) * mm, "end": v(-24.2, 11.61) * mm});
            skLineSegment(sketch, "E58.5.4", {"start": v(-24.22, 12.07) * mm, "end": v(-24.12, 12.3) * mm});
            skLineSegment(sketch, "E58.5.5", {"start": v(-24, 12.5) * mm, "end": v(-24.12, 12.3) * mm});
            skArc(sketch, "E58.5.6", {"start": v(-23.61, 12.75) * mm, "mid": v(-23.84, 12.67) * mm, "end": v(-24, 12.5) * mm});
            skArc(sketch, "E58.5.7", {"start": v(-22, 12.7) * mm, "mid": v(-22.8, 12.77) * mm, "end": v(-23.61, 12.75) * mm});
            skLineSegment(sketch, "E58.5.8", {"start": v(-22, 12.7) * mm, "end": v(-20.9, 12.06) * mm});
            skArc(sketch, "E58.5.9", {"start": v(-20.9, 12.06) * mm, "mid": v(-20.51, 12.01) * mm, "end": v(-20.2, 12.24) * mm});
            skArc(sketch, "E58.6.0", {"start": v(-23.2, 4.42) * mm, "mid": v(-23.28, 4.8) * mm, "end": v(-23.6, 5.02) * mm});
            skLineSegment(sketch, "E58.6.1", {"start": v(-24.84, 5.28) * mm, "end": v(-23.6, 5.02) * mm});
            skArc(sketch, "E58.6.2", {"start": v(-24.84, 5.28) * mm, "mid": v(-25.5, 5.77) * mm, "end": v(-26.08, 6.33) * mm});
            skArc(sketch, "E58.6.3", {"start": v(-26.2, 6.78) * mm, "mid": v(-26.2, 6.54) * mm, "end": v(-26.08, 6.33) * mm});
            skLineSegment(sketch, "E58.6.4", {"start": v(-26.2, 6.78) * mm, "end": v(-26.15, 7) * mm});
            skLineSegment(sketch, "E58.6.5", {"start": v(-26.08, 7.23) * mm, "end": v(-26.15, 7) * mm});
            skArc(sketch, "E58.6.6", {"start": v(-25.75, 7.56) * mm, "mid": v(-25.95, 7.43) * mm, "end": v(-26.08, 7.23) * mm});
            skArc(sketch, "E58.6.7", {"start": v(-24.16, 7.85) * mm, "mid": v(-24.96, 7.75) * mm, "end": v(-25.75, 7.56) * mm});
            skLineSegment(sketch, "E58.6.8", {"start": v(-24.16, 7.85) * mm, "end": v(-22.94, 7.45) * mm});
            skArc(sketch, "E58.6.9", {"start": v(-22.94, 7.45) * mm, "mid": v(-22.56, 7.48) * mm, "end": v(-22.3, 7.77) * mm});
            skArc(sketch, "E58.7.0", {"start": v(-23.62, -0.5) * mm, "mid": v(-23.77, -0.15) * mm, "end": v(-24.12, 0) * mm});
            skLineSegment(sketch, "E58.7.1", {"start": v(-25.4, 0) * mm, "end": v(-24.12, 0) * mm});
            skArc(sketch, "E58.7.2", {"start": v(-25.4, 0) * mm, "mid": v(-26.14, 0.34) * mm, "end": v(-26.82, 0.77) * mm});
            skArc(sketch, "E58.7.3", {"start": v(-27.04, 1.18) * mm, "mid": v(-26.98, 0.95) * mm, "end": v(-26.82, 0.77) * mm});
            skLineSegment(sketch, "E58.7.4", {"start": v(-27.04, 1.18) * mm, "end": v(-27.04, 1.42) * mm});
            skLineSegment(sketch, "E58.7.5", {"start": v(-27.01, 1.65) * mm, "end": v(-27.04, 1.42) * mm});
            skArc(sketch, "E58.7.6", {"start": v(-26.76, 2.04) * mm, "mid": v(-26.93, 1.88) * mm, "end": v(-27.01, 1.65) * mm});
            skArc(sketch, "E58.7.7", {"start": v(-25.26, 2.66) * mm, "mid": v(-26.03, 2.4) * mm, "end": v(-26.76, 2.04) * mm});
            skLineSegment(sketch, "E58.7.8", {"start": v(-25.26, 2.66) * mm, "end": v(-24, 2.52) * mm});
            skArc(sketch, "E58.7.9", {"start": v(-24, 2.52) * mm, "mid": v(-23.62, 2.63) * mm, "end": v(-23.44, 2.96) * mm});
            skArc(sketch, "E58.8.0", {"start": v(-23, -5.4) * mm, "mid": v(-23.22, -5.08) * mm, "end": v(-23.6, -5.02) * mm});
            skLineSegment(sketch, "E58.8.1", {"start": v(-24.84, -5.28) * mm, "end": v(-23.6, -5.02) * mm});
            skArc(sketch, "E58.8.2", {"start": v(-24.84, -5.28) * mm, "mid": v(-25.64, -5.1) * mm, "end": v(-26.4, -4.83) * mm});
            skArc(sketch, "E58.8.3", {"start": v(-26.69, -4.47) * mm, "mid": v(-26.59, -4.68) * mm, "end": v(-26.4, -4.83) * mm});
            skLineSegment(sketch, "E58.8.4", {"start": v(-26.69, -4.47) * mm, "end": v(-26.74, -4.24) * mm});
            skLineSegment(sketch, "E58.8.5", {"start": v(-26.76, -4) * mm, "end": v(-26.74, -4.24) * mm});
            skArc(sketch, "E58.8.6", {"start": v(-26.6, -3.57) * mm, "mid": v(-26.73, -3.76) * mm, "end": v(-26.76, -4) * mm});
            skArc(sketch, "E58.8.7", {"start": v(-25.26, -2.66) * mm, "mid": v(-25.96, -3.07) * mm, "end": v(-26.6, -3.57) * mm});
            skLineSegment(sketch, "E58.8.8", {"start": v(-25.26, -2.66) * mm, "end": v(-24, -2.52) * mm});
            skArc(sketch, "E58.8.9", {"start": v(-24, -2.52) * mm, "mid": v(-23.65, -2.34) * mm, "end": v(-23.54, -1.97) * mm});
            skArc(sketch, "E58.9.0", {"start": v(-21.37, -10.06) * mm, "mid": v(-21.66, -9.8) * mm, "end": v(-22.04, -9.81) * mm});
            skLineSegment(sketch, "E58.9.1", {"start": v(-23.2, -10.33) * mm, "end": v(-22.04, -9.81) * mm});
            skArc(sketch, "E58.9.2", {"start": v(-23.2, -10.33) * mm, "mid": v(-24.01, -10.32) * mm, "end": v(-24.82, -10.2) * mm});
            skArc(sketch, "E58.9.3", {"start": v(-25.18, -9.92) * mm, "mid": v(-25.03, -10.1) * mm, "end": v(-24.82, -10.2) * mm});
            skLineSegment(sketch, "E58.9.4", {"start": v(-25.18, -9.92) * mm, "end": v(-25.27, -9.7) * mm});
            skLineSegment(sketch, "E58.9.5", {"start": v(-25.35, -9.48) * mm, "end": v(-25.27, -9.7) * mm});
            skArc(sketch, "E58.9.6", {"start": v(-25.27, -9.02) * mm, "mid": v(-25.37, -9.24) * mm, "end": v(-25.35, -9.48) * mm});
            skArc(sketch, "E58.9.7", {"start": v(-24.16, -7.85) * mm, "mid": v(-24.75, -8.4) * mm, "end": v(-25.27, -9.02) * mm});
            skLineSegment(sketch, "E58.9.8", {"start": v(-24.16, -7.85) * mm, "end": v(-22.94, -7.45) * mm});
            skArc(sketch, "E58.9.9", {"start": v(-22.94, -7.45) * mm, "mid": v(-22.65, -7.2) * mm, "end": v(-22.61, -6.83) * mm});
            skArc(sketch, "E58.10.0", {"start": v(-18.81, -14.28) * mm, "mid": v(-19.14, -14.09) * mm, "end": v(-19.52, -14.18) * mm});
            skLineSegment(sketch, "E58.10.1", {"start": v(-20.55, -14.93) * mm, "end": v(-19.52, -14.18) * mm});
            skArc(sketch, "E58.10.2", {"start": v(-20.55, -14.93) * mm, "mid": v(-21.34, -15.09) * mm, "end": v(-22.15, -15.14) * mm});
            skArc(sketch, "E58.10.3", {"start": v(-22.57, -14.94) * mm, "mid": v(-22.38, -15.1) * mm, "end": v(-22.15, -15.14) * mm});
            skLineSegment(sketch, "E58.10.4", {"start": v(-22.57, -14.94) * mm, "end": v(-22.7, -14.74) * mm});
            skLineSegment(sketch, "E58.10.5", {"start": v(-22.82, -14.54) * mm, "end": v(-22.7, -14.74) * mm});
            skArc(sketch, "E58.10.6", {"start": v(-22.85, -14.08) * mm, "mid": v(-22.9, -14.31) * mm, "end": v(-22.82, -14.54) * mm});
            skArc(sketch, "E58.10.7", {"start": v(-22, -12.7) * mm, "mid": v(-22.47, -13.36) * mm, "end": v(-22.85, -14.08) * mm});
            skLineSegment(sketch, "E58.10.8", {"start": v(-22, -12.7) * mm, "end": v(-20.9, -12.06) * mm});
            skArc(sketch, "E58.10.9", {"start": v(-20.9, -12.06) * mm, "mid": v(-20.66, -11.76) * mm, "end": v(-20.7, -11.38) * mm});
            skArc(sketch, "E58.11.0", {"start": v(-15.43, -17.88) * mm, "mid": v(-15.8, -17.76) * mm, "end": v(-16.14, -17.93) * mm});
            skLineSegment(sketch, "E58.11.1", {"start": v(-17, -18.88) * mm, "end": v(-16.14, -17.93) * mm});
            skArc(sketch, "E58.11.2", {"start": v(-17, -18.88) * mm, "mid": v(-17.74, -19.2) * mm, "end": v(-18.52, -19.42) * mm});
            skArc(sketch, "E58.11.3", {"start": v(-18.97, -19.3) * mm, "mid": v(-18.76, -19.41) * mm, "end": v(-18.52, -19.42) * mm});
            skLineSegment(sketch, "E58.11.4", {"start": v(-18.97, -19.3) * mm, "end": v(-19.14, -19.14) * mm});
            skLineSegment(sketch, "E58.11.5", {"start": v(-19.3, -18.97) * mm, "end": v(-19.14, -19.14) * mm});
            skArc(sketch, "E58.11.6", {"start": v(-19.42, -18.52) * mm, "mid": v(-19.41, -18.76) * mm, "end": v(-19.3, -18.97) * mm});
            skArc(sketch, "E58.11.7", {"start": v(-18.88, -17) * mm, "mid": v(-19.2, -17.74) * mm, "end": v(-19.42, -18.52) * mm});
            skLineSegment(sketch, "E58.11.8", {"start": v(-18.88, -17) * mm, "end": v(-17.93, -16.14) * mm});
            skArc(sketch, "E58.11.9", {"start": v(-17.93, -16.14) * mm, "mid": v(-17.76, -15.8) * mm, "end": v(-17.88, -15.43) * mm});
            skArc(sketch, "E58.12.0", {"start": v(-11.38, -20.7) * mm, "mid": v(-11.76, -20.66) * mm, "end": v(-12.06, -20.9) * mm});
            skLineSegment(sketch, "E58.12.1", {"start": v(-12.7, -22) * mm, "end": v(-12.06, -20.9) * mm});
            skArc(sketch, "E58.12.2", {"start": v(-12.7, -22) * mm, "mid": v(-13.36, -22.47) * mm, "end": v(-14.08, -22.85) * mm});
            skArc(sketch, "E58.12.3", {"start": v(-14.54, -22.82) * mm, "mid": v(-14.31, -22.9) * mm, "end": v(-14.08, -22.85) * mm});
            skLineSegment(sketch, "E58.12.4", {"start": v(-14.54, -22.82) * mm, "end": v(-14.74, -22.7) * mm});
            skLineSegment(sketch, "E58.12.5", {"start": v(-14.94, -22.57) * mm, "end": v(-14.74, -22.7) * mm});
            skArc(sketch, "E58.12.6", {"start": v(-15.14, -22.15) * mm, "mid": v(-15.1, -22.38) * mm, "end": v(-14.94, -22.57) * mm});
            skArc(sketch, "E58.12.7", {"start": v(-14.93, -20.55) * mm, "mid": v(-15.09, -21.34) * mm, "end": v(-15.14, -22.15) * mm});
            skLineSegment(sketch, "E58.12.8", {"start": v(-14.93, -20.55) * mm, "end": v(-14.18, -19.52) * mm});
            skArc(sketch, "E58.12.9", {"start": v(-14.18, -19.52) * mm, "mid": v(-14.09, -19.14) * mm, "end": v(-14.28, -18.81) * mm});
            skArc(sketch, "E58.13.0", {"start": v(-6.83, -22.61) * mm, "mid": v(-7.2, -22.65) * mm, "end": v(-7.45, -22.94) * mm});
            skLineSegment(sketch, "E58.13.1", {"start": v(-7.85, -24.16) * mm, "end": v(-7.45, -22.94) * mm});
            skArc(sketch, "E58.13.2", {"start": v(-7.85, -24.16) * mm, "mid": v(-8.4, -24.75) * mm, "end": v(-9.02, -25.27) * mm});
            skArc(sketch, "E58.13.3", {"start": v(-9.48, -25.35) * mm, "mid": v(-9.24, -25.37) * mm, "end": v(-9.02, -25.27) * mm});
            skLineSegment(sketch, "E58.13.4", {"start": v(-9.48, -25.35) * mm, "end": v(-9.7, -25.27) * mm});
            skLineSegment(sketch, "E58.13.5", {"start": v(-9.92, -25.18) * mm, "end": v(-9.7, -25.27) * mm});
            skArc(sketch, "E58.13.6", {"start": v(-10.2, -24.82) * mm, "mid": v(-10.1, -25.03) * mm, "end": v(-9.92, -25.18) * mm});
            skArc(sketch, "E58.13.7", {"start": v(-10.33, -23.2) * mm, "mid": v(-10.32, -24.01) * mm, "end": v(-10.2, -24.82) * mm});
            skLineSegment(sketch, "E58.13.8", {"start": v(-10.33, -23.2) * mm, "end": v(-9.81, -22.04) * mm});
            skArc(sketch, "E58.13.9", {"start": v(-9.81, -22.04) * mm, "mid": v(-9.8, -21.66) * mm, "end": v(-10.06, -21.37) * mm});
            skArc(sketch, "E58.14.0", {"start": v(-1.97, -23.54) * mm, "mid": v(-2.34, -23.65) * mm, "end": v(-2.52, -24) * mm});
            skLineSegment(sketch, "E58.14.1", {"start": v(-2.66, -25.26) * mm, "end": v(-2.52, -24) * mm});
            skArc(sketch, "E58.14.2", {"start": v(-2.66, -25.26) * mm, "mid": v(-3.07, -25.96) * mm, "end": v(-3.57, -26.6) * mm});
            skArc(sketch, "E58.14.3", {"start": v(-4, -26.76) * mm, "mid": v(-3.76, -26.73) * mm, "end": v(-3.57, -26.6) * mm});
            skLineSegment(sketch, "E58.14.4", {"start": v(-4, -26.76) * mm, "end": v(-4.24, -26.74) * mm});
            skLineSegment(sketch, "E58.14.5", {"start": v(-4.47, -26.69) * mm, "end": v(-4.24, -26.74) * mm});
            skArc(sketch, "E58.14.6", {"start": v(-4.83, -26.4) * mm, "mid": v(-4.68, -26.59) * mm, "end": v(-4.47, -26.69) * mm});
            skArc(sketch, "E58.14.7", {"start": v(-5.28, -24.84) * mm, "mid": v(-5.1, -25.64) * mm, "end": v(-4.83, -26.4) * mm});
            skLineSegment(sketch, "E58.14.8", {"start": v(-5.28, -24.84) * mm, "end": v(-5.02, -23.6) * mm});
            skArc(sketch, "E58.14.9", {"start": v(-5.02, -23.6) * mm, "mid": v(-5.08, -23.22) * mm, "end": v(-5.4, -23) * mm});
            skArc(sketch, "E58.15.0", {"start": v(2.96, -23.44) * mm, "mid": v(2.63, -23.62) * mm, "end": v(2.52, -24) * mm});
            skLineSegment(sketch, "E58.15.1", {"start": v(2.66, -25.26) * mm, "end": v(2.52, -24) * mm});
            skArc(sketch, "E58.15.2", {"start": v(2.66, -25.26) * mm, "mid": v(2.4, -26.03) * mm, "end": v(2.04, -26.76) * mm});
            skArc(sketch, "E58.15.3", {"start": v(1.65, -27.01) * mm, "mid": v(1.88, -26.93) * mm, "end": v(2.04, -26.76) * mm});
            skLineSegment(sketch, "E58.15.4", {"start": v(1.65, -27.01) * mm, "end": v(1.42, -27.04) * mm});
            skLineSegment(sketch, "E58.15.5", {"start": v(1.18, -27.04) * mm, "end": v(1.42, -27.04) * mm});
            skArc(sketch, "E58.15.6", {"start": v(0.77, -26.82) * mm, "mid": v(0.95, -26.98) * mm, "end": v(1.18, -27.04) * mm});
            skArc(sketch, "E58.15.7", {"start": v(0, -25.4) * mm, "mid": v(0.34, -26.14) * mm, "end": v(0.77, -26.82) * mm});
            skLineSegment(sketch, "E58.15.8", {"start": v(0, -25.4) * mm, "end": v(0, -24.12) * mm});
            skArc(sketch, "E58.15.9", {"start": v(0, -24.12) * mm, "mid": v(-0.15, -23.77) * mm, "end": v(-0.5, -23.62) * mm});
            skArc(sketch, "E58.16.0", {"start": v(7.77, -22.3) * mm, "mid": v(7.48, -22.56) * mm, "end": v(7.45, -22.94) * mm});
            skLineSegment(sketch, "E58.16.1", {"start": v(7.85, -24.16) * mm, "end": v(7.45, -22.94) * mm});
            skArc(sketch, "E58.16.2", {"start": v(7.85, -24.16) * mm, "mid": v(7.75, -24.96) * mm, "end": v(7.56, -25.75) * mm});
            skArc(sketch, "E58.16.3", {"start": v(7.23, -26.08) * mm, "mid": v(7.43, -25.95) * mm, "end": v(7.56, -25.75) * mm});
            skLineSegment(sketch, "E58.16.4", {"start": v(7.23, -26.08) * mm, "end": v(7, -26.15) * mm});
            skLineSegment(sketch, "E58.16.5", {"start": v(6.78, -26.2) * mm, "end": v(7, -26.15) * mm});
            skArc(sketch, "E58.16.6", {"start": v(6.33, -26.08) * mm, "mid": v(6.54, -26.2) * mm, "end": v(6.78, -26.2) * mm});
            skArc(sketch, "E58.16.7", {"start": v(5.28, -24.84) * mm, "mid": v(5.77, -25.5) * mm, "end": v(6.33, -26.08) * mm});
            skLineSegment(sketch, "E58.16.8", {"start": v(5.28, -24.84) * mm, "end": v(5.02, -23.6) * mm});
            skArc(sketch, "E58.16.9", {"start": v(5.02, -23.6) * mm, "mid": v(4.8, -23.28) * mm, "end": v(4.42, -23.2) * mm});
            skArc(sketch, "E58.17.0", {"start": v(12.24, -20.2) * mm, "mid": v(12.01, -20.51) * mm, "end": v(12.06, -20.9) * mm});
            skLineSegment(sketch, "E58.17.1", {"start": v(12.7, -22) * mm, "end": v(12.06, -20.9) * mm});
            skArc(sketch, "E58.17.2", {"start": v(12.7, -22) * mm, "mid": v(12.77, -22.8) * mm, "end": v(12.75, -23.61) * mm});
            skArc(sketch, "E58.17.3", {"start": v(12.5, -24) * mm, "mid": v(12.67, -23.84) * mm, "end": v(12.75, -23.61) * mm});
            skLineSegment(sketch, "E58.17.4", {"start": v(12.5, -24) * mm, "end": v(12.3, -24.12) * mm});
            skLineSegment(sketch, "E58.17.5", {"start": v(12.07, -24.22) * mm, "end": v(12.3, -24.12) * mm});
            skArc(sketch, "E58.17.6", {"start": v(11.61, -24.2) * mm, "mid": v(11.84, -24.26) * mm, "end": v(12.07, -24.22) * mm});
            skArc(sketch, "E58.17.7", {"start": v(10.33, -23.2) * mm, "mid": v(10.94, -23.74) * mm, "end": v(11.61, -24.2) * mm});
            skLineSegment(sketch, "E58.17.8", {"start": v(10.33, -23.2) * mm, "end": v(9.81, -22.04) * mm});
            skArc(sketch, "E58.17.9", {"start": v(9.81, -22.04) * mm, "mid": v(9.54, -21.77) * mm, "end": v(9.15, -21.78) * mm});
            skArc(sketch, "E58.18.0", {"start": v(16.17, -17.22) * mm, "mid": v(16.01, -17.57) * mm, "end": v(16.14, -17.93) * mm});
            skLineSegment(sketch, "E58.18.1", {"start": v(17, -18.88) * mm, "end": v(16.14, -17.93) * mm});
            skArc(sketch, "E58.18.2", {"start": v(17, -18.88) * mm, "mid": v(17.24, -19.65) * mm, "end": v(17.38, -20.45) * mm});
            skArc(sketch, "E58.18.3", {"start": v(17.21, -20.88) * mm, "mid": v(17.35, -20.68) * mm, "end": v(17.38, -20.45) * mm});
            skLineSegment(sketch, "E58.18.4", {"start": v(17.21, -20.88) * mm, "end": v(17.04, -21.04) * mm});
            skLineSegment(sketch, "E58.18.5", {"start": v(16.85, -21.18) * mm, "end": v(17.04, -21.04) * mm});
            skArc(sketch, "E58.18.6", {"start": v(16.39, -21.25) * mm, "mid": v(16.63, -21.27) * mm, "end": v(16.85, -21.18) * mm});
            skArc(sketch, "E58.18.7", {"start": v(14.93, -20.55) * mm, "mid": v(15.64, -20.95) * mm, "end": v(16.39, -21.25) * mm});
            skLineSegment(sketch, "E58.18.8", {"start": v(14.93, -20.55) * mm, "end": v(14.18, -19.52) * mm});
            skArc(sketch, "E58.18.9", {"start": v(14.18, -19.52) * mm, "mid": v(13.85, -19.31) * mm, "end": v(13.48, -19.4) * mm});
            skArc(sketch, "E58.19.0", {"start": v(19.4, -13.48) * mm, "mid": v(19.31, -13.85) * mm, "end": v(19.52, -14.18) * mm});
            skLineSegment(sketch, "E58.19.1", {"start": v(20.55, -14.93) * mm, "end": v(19.52, -14.18) * mm});
            skArc(sketch, "E58.19.2", {"start": v(20.55, -14.93) * mm, "mid": v(20.95, -15.64) * mm, "end": v(21.25, -16.39) * mm});
            skArc(sketch, "E58.19.3", {"start": v(21.18, -16.85) * mm, "mid": v(21.27, -16.63) * mm, "end": v(21.25, -16.39) * mm});
            skLineSegment(sketch, "E58.19.4", {"start": v(21.18, -16.85) * mm, "end": v(21.04, -17.04) * mm});
            skLineSegment(sketch, "E58.19.5", {"start": v(20.88, -17.21) * mm, "end": v(21.04, -17.04) * mm});
            skArc(sketch, "E58.19.6", {"start": v(20.45, -17.38) * mm, "mid": v(20.68, -17.35) * mm, "end": v(20.88, -17.21) * mm});
            skArc(sketch, "E58.19.7", {"start": v(18.88, -17) * mm, "mid": v(19.65, -17.24) * mm, "end": v(20.45, -17.38) * mm});
            skLineSegment(sketch, "E58.19.8", {"start": v(18.88, -17) * mm, "end": v(17.93, -16.14) * mm});
            skArc(sketch, "E58.19.9", {"start": v(17.93, -16.14) * mm, "mid": v(17.57, -16.01) * mm, "end": v(17.22, -16.17) * mm});
            skArc(sketch, "E58.20.0", {"start": v(21.78, -9.15) * mm, "mid": v(21.77, -9.54) * mm, "end": v(22.04, -9.81) * mm});
            skLineSegment(sketch, "E58.20.1", {"start": v(23.2, -10.33) * mm, "end": v(22.04, -9.81) * mm});
            skArc(sketch, "E58.20.2", {"start": v(23.2, -10.33) * mm, "mid": v(23.74, -10.94) * mm, "end": v(24.2, -11.61) * mm});
            skArc(sketch, "E58.20.3", {"start": v(24.22, -12.07) * mm, "mid": v(24.26, -11.84) * mm, "end": v(24.2, -11.61) * mm});
            skLineSegment(sketch, "E58.20.4", {"start": v(24.22, -12.07) * mm, "end": v(24.12, -12.3) * mm});
            skLineSegment(sketch, "E58.20.5", {"start": v(24, -12.5) * mm, "end": v(24.12, -12.3) * mm});
            skArc(sketch, "E58.20.6", {"start": v(23.61, -12.75) * mm, "mid": v(23.84, -12.67) * mm, "end": v(24, -12.5) * mm});
            skArc(sketch, "E58.20.7", {"start": v(22, -12.7) * mm, "mid": v(22.8, -12.77) * mm, "end": v(23.61, -12.75) * mm});
            skLineSegment(sketch, "E58.20.8", {"start": v(22, -12.7) * mm, "end": v(20.9, -12.06) * mm});
            skArc(sketch, "E58.20.9", {"start": v(20.9, -12.06) * mm, "mid": v(20.51, -12.01) * mm, "end": v(20.2, -12.24) * mm});
            skArc(sketch, "E58.21.0", {"start": v(23.2, -4.42) * mm, "mid": v(23.28, -4.8) * mm, "end": v(23.6, -5.02) * mm});
            skLineSegment(sketch, "E58.21.1", {"start": v(24.84, -5.28) * mm, "end": v(23.6, -5.02) * mm});
            skArc(sketch, "E58.21.2", {"start": v(24.84, -5.28) * mm, "mid": v(25.5, -5.77) * mm, "end": v(26.08, -6.33) * mm});
            skArc(sketch, "E58.21.3", {"start": v(26.2, -6.78) * mm, "mid": v(26.2, -6.54) * mm, "end": v(26.08, -6.33) * mm});
            skLineSegment(sketch, "E58.21.4", {"start": v(26.2, -6.78) * mm, "end": v(26.15, -7) * mm});
            skLineSegment(sketch, "E58.21.5", {"start": v(26.08, -7.23) * mm, "end": v(26.15, -7) * mm});
            skArc(sketch, "E58.21.6", {"start": v(25.75, -7.56) * mm, "mid": v(25.95, -7.43) * mm, "end": v(26.08, -7.23) * mm});
            skArc(sketch, "E58.21.7", {"start": v(24.16, -7.85) * mm, "mid": v(24.96, -7.75) * mm, "end": v(25.75, -7.56) * mm});
            skLineSegment(sketch, "E58.21.8", {"start": v(24.16, -7.85) * mm, "end": v(22.94, -7.45) * mm});
            skArc(sketch, "E58.21.9", {"start": v(22.94, -7.45) * mm, "mid": v(22.56, -7.48) * mm, "end": v(22.3, -7.77) * mm});
            skArc(sketch, "E58.22.0", {"start": v(23.62, 0.5) * mm, "mid": v(23.77, 0.15) * mm, "end": v(24.12, 0) * mm});
            skLineSegment(sketch, "E58.22.1", {"start": v(25.4, 0) * mm, "end": v(24.12, 0) * mm});
            skArc(sketch, "E58.22.2", {"start": v(25.4, 0) * mm, "mid": v(26.14, -0.34) * mm, "end": v(26.82, -0.77) * mm});
            skArc(sketch, "E58.22.3", {"start": v(27.04, -1.18) * mm, "mid": v(26.98, -0.95) * mm, "end": v(26.82, -0.77) * mm});
            skLineSegment(sketch, "E58.22.4", {"start": v(27.04, -1.18) * mm, "end": v(27.04, -1.42) * mm});
            skLineSegment(sketch, "E58.22.5", {"start": v(27.01, -1.65) * mm, "end": v(27.04, -1.42) * mm});
            skArc(sketch, "E58.22.6", {"start": v(26.76, -2.04) * mm, "mid": v(26.93, -1.88) * mm, "end": v(27.01, -1.65) * mm});
            skArc(sketch, "E58.22.7", {"start": v(25.26, -2.66) * mm, "mid": v(26.03, -2.4) * mm, "end": v(26.76, -2.04) * mm});
            skLineSegment(sketch, "E58.22.8", {"start": v(25.26, -2.66) * mm, "end": v(24, -2.52) * mm});
            skArc(sketch, "E58.22.9", {"start": v(24, -2.52) * mm, "mid": v(23.62, -2.63) * mm, "end": v(23.44, -2.96) * mm});
            skArc(sketch, "E58.23.0", {"start": v(23, 5.4) * mm, "mid": v(23.22, 5.08) * mm, "end": v(23.6, 5.02) * mm});
            skLineSegment(sketch, "E58.23.1", {"start": v(24.84, 5.28) * mm, "end": v(23.6, 5.02) * mm});
            skArc(sketch, "E58.23.2", {"start": v(24.84, 5.28) * mm, "mid": v(25.64, 5.1) * mm, "end": v(26.4, 4.83) * mm});
            skArc(sketch, "E58.23.3", {"start": v(26.69, 4.47) * mm, "mid": v(26.59, 4.68) * mm, "end": v(26.4, 4.83) * mm});
            skLineSegment(sketch, "E58.23.4", {"start": v(26.69, 4.47) * mm, "end": v(26.74, 4.24) * mm});
            skLineSegment(sketch, "E58.23.5", {"start": v(26.76, 4) * mm, "end": v(26.74, 4.24) * mm});
            skArc(sketch, "E58.23.6", {"start": v(26.6, 3.57) * mm, "mid": v(26.73, 3.76) * mm, "end": v(26.76, 4) * mm});
            skArc(sketch, "E58.23.7", {"start": v(25.26, 2.66) * mm, "mid": v(25.96, 3.07) * mm, "end": v(26.6, 3.57) * mm});
            skLineSegment(sketch, "E58.23.8", {"start": v(25.26, 2.66) * mm, "end": v(24, 2.52) * mm});
            skArc(sketch, "E58.23.9", {"start": v(24, 2.52) * mm, "mid": v(23.65, 2.34) * mm, "end": v(23.54, 1.97) * mm});
            skArc(sketch, "E58.24.0", {"start": v(21.37, 10.06) * mm, "mid": v(21.66, 9.8) * mm, "end": v(22.04, 9.81) * mm});
            skLineSegment(sketch, "E58.24.1", {"start": v(23.2, 10.33) * mm, "end": v(22.04, 9.81) * mm});
            skArc(sketch, "E58.24.2", {"start": v(23.2, 10.33) * mm, "mid": v(24.01, 10.32) * mm, "end": v(24.82, 10.2) * mm});
            skArc(sketch, "E58.24.3", {"start": v(25.18, 9.92) * mm, "mid": v(25.03, 10.1) * mm, "end": v(24.82, 10.2) * mm});
            skLineSegment(sketch, "E58.24.4", {"start": v(25.18, 9.92) * mm, "end": v(25.27, 9.7) * mm});
            skLineSegment(sketch, "E58.24.5", {"start": v(25.35, 9.48) * mm, "end": v(25.27, 9.7) * mm});
            skArc(sketch, "E58.24.6", {"start": v(25.27, 9.02) * mm, "mid": v(25.37, 9.24) * mm, "end": v(25.35, 9.48) * mm});
            skArc(sketch, "E58.24.7", {"start": v(24.16, 7.85) * mm, "mid": v(24.75, 8.4) * mm, "end": v(25.27, 9.02) * mm});
            skLineSegment(sketch, "E58.24.8", {"start": v(24.16, 7.85) * mm, "end": v(22.94, 7.45) * mm});
            skArc(sketch, "E58.24.9", {"start": v(22.94, 7.45) * mm, "mid": v(22.65, 7.2) * mm, "end": v(22.61, 6.83) * mm});
            skArc(sketch, "E58.25.0", {"start": v(18.81, 14.28) * mm, "mid": v(19.14, 14.09) * mm, "end": v(19.52, 14.18) * mm});
            skLineSegment(sketch, "E58.25.1", {"start": v(20.55, 14.93) * mm, "end": v(19.52, 14.18) * mm});
            skArc(sketch, "E58.25.2", {"start": v(20.55, 14.93) * mm, "mid": v(21.34, 15.09) * mm, "end": v(22.15, 15.14) * mm});
            skArc(sketch, "E58.25.3", {"start": v(22.57, 14.94) * mm, "mid": v(22.38, 15.1) * mm, "end": v(22.15, 15.14) * mm});
            skLineSegment(sketch, "E58.25.4", {"start": v(22.57, 14.94) * mm, "end": v(22.7, 14.74) * mm});
            skLineSegment(sketch, "E58.25.5", {"start": v(22.82, 14.54) * mm, "end": v(22.7, 14.74) * mm});
            skArc(sketch, "E58.25.6", {"start": v(22.85, 14.08) * mm, "mid": v(22.9, 14.31) * mm, "end": v(22.82, 14.54) * mm});
            skArc(sketch, "E58.25.7", {"start": v(22, 12.7) * mm, "mid": v(22.47, 13.36) * mm, "end": v(22.85, 14.08) * mm});
            skLineSegment(sketch, "E58.25.8", {"start": v(22, 12.7) * mm, "end": v(20.9, 12.06) * mm});
            skArc(sketch, "E58.25.9", {"start": v(20.9, 12.06) * mm, "mid": v(20.66, 11.76) * mm, "end": v(20.7, 11.38) * mm});
            skArc(sketch, "E58.26.0", {"start": v(15.43, 17.88) * mm, "mid": v(15.8, 17.76) * mm, "end": v(16.14, 17.93) * mm});
            skLineSegment(sketch, "E58.26.1", {"start": v(17, 18.88) * mm, "end": v(16.14, 17.93) * mm});
            skArc(sketch, "E58.26.2", {"start": v(17, 18.88) * mm, "mid": v(17.74, 19.2) * mm, "end": v(18.52, 19.42) * mm});
            skArc(sketch, "E58.26.3", {"start": v(18.97, 19.3) * mm, "mid": v(18.76, 19.41) * mm, "end": v(18.52, 19.42) * mm});
            skLineSegment(sketch, "E58.26.4", {"start": v(18.97, 19.3) * mm, "end": v(19.14, 19.14) * mm});
            skLineSegment(sketch, "E58.26.5", {"start": v(19.3, 18.97) * mm, "end": v(19.14, 19.14) * mm});
            skArc(sketch, "E58.26.6", {"start": v(19.42, 18.52) * mm, "mid": v(19.41, 18.76) * mm, "end": v(19.3, 18.97) * mm});
            skArc(sketch, "E58.26.7", {"start": v(18.88, 17) * mm, "mid": v(19.2, 17.74) * mm, "end": v(19.42, 18.52) * mm});
            skLineSegment(sketch, "E58.26.8", {"start": v(18.88, 17) * mm, "end": v(17.93, 16.14) * mm});
            skArc(sketch, "E58.26.9", {"start": v(17.93, 16.14) * mm, "mid": v(17.76, 15.8) * mm, "end": v(17.88, 15.43) * mm});
            skArc(sketch, "E58.27.0", {"start": v(11.38, 20.7) * mm, "mid": v(11.76, 20.66) * mm, "end": v(12.06, 20.9) * mm});
            skLineSegment(sketch, "E58.27.1", {"start": v(12.7, 22) * mm, "end": v(12.06, 20.9) * mm});
            skArc(sketch, "E58.27.2", {"start": v(12.7, 22) * mm, "mid": v(13.36, 22.47) * mm, "end": v(14.08, 22.85) * mm});
            skArc(sketch, "E58.27.3", {"start": v(14.54, 22.82) * mm, "mid": v(14.31, 22.9) * mm, "end": v(14.08, 22.85) * mm});
            skLineSegment(sketch, "E58.27.4", {"start": v(14.54, 22.82) * mm, "end": v(14.74, 22.7) * mm});
            skLineSegment(sketch, "E58.27.5", {"start": v(14.94, 22.57) * mm, "end": v(14.74, 22.7) * mm});
            skArc(sketch, "E58.27.6", {"start": v(15.14, 22.15) * mm, "mid": v(15.1, 22.38) * mm, "end": v(14.94, 22.57) * mm});
            skArc(sketch, "E58.27.7", {"start": v(14.93, 20.55) * mm, "mid": v(15.09, 21.34) * mm, "end": v(15.14, 22.15) * mm});
            skLineSegment(sketch, "E58.27.8", {"start": v(14.93, 20.55) * mm, "end": v(14.18, 19.52) * mm});
            skArc(sketch, "E58.27.9", {"start": v(14.18, 19.52) * mm, "mid": v(14.09, 19.14) * mm, "end": v(14.28, 18.81) * mm});
            skArc(sketch, "E58.28.0", {"start": v(6.83, 22.61) * mm, "mid": v(7.2, 22.65) * mm, "end": v(7.45, 22.94) * mm});
            skLineSegment(sketch, "E58.28.1", {"start": v(7.85, 24.16) * mm, "end": v(7.45, 22.94) * mm});
            skArc(sketch, "E58.28.2", {"start": v(7.85, 24.16) * mm, "mid": v(8.4, 24.75) * mm, "end": v(9.02, 25.27) * mm});
            skArc(sketch, "E58.28.3", {"start": v(9.48, 25.35) * mm, "mid": v(9.24, 25.37) * mm, "end": v(9.02, 25.27) * mm});
            skLineSegment(sketch, "E58.28.4", {"start": v(9.48, 25.35) * mm, "end": v(9.7, 25.27) * mm});
            skLineSegment(sketch, "E58.28.5", {"start": v(9.92, 25.18) * mm, "end": v(9.7, 25.27) * mm});
            skArc(sketch, "E58.28.6", {"start": v(10.2, 24.82) * mm, "mid": v(10.1, 25.03) * mm, "end": v(9.92, 25.18) * mm});
            skArc(sketch, "E58.28.7", {"start": v(10.33, 23.2) * mm, "mid": v(10.32, 24.01) * mm, "end": v(10.2, 24.82) * mm});
            skLineSegment(sketch, "E58.28.8", {"start": v(10.33, 23.2) * mm, "end": v(9.81, 22.04) * mm});
            skArc(sketch, "E58.28.9", {"start": v(9.81, 22.04) * mm, "mid": v(9.8, 21.66) * mm, "end": v(10.06, 21.37) * mm});
            skArc(sketch, "E58.29.0", {"start": v(1.97, 23.54) * mm, "mid": v(2.34, 23.65) * mm, "end": v(2.52, 24) * mm});
            skLineSegment(sketch, "E58.29.1", {"start": v(2.66, 25.26) * mm, "end": v(2.52, 24) * mm});
            skArc(sketch, "E58.29.2", {"start": v(2.66, 25.26) * mm, "mid": v(3.07, 25.96) * mm, "end": v(3.57, 26.6) * mm});
            skArc(sketch, "E58.29.3", {"start": v(4, 26.76) * mm, "mid": v(3.76, 26.73) * mm, "end": v(3.57, 26.6) * mm});
            skLineSegment(sketch, "E58.29.4", {"start": v(4, 26.76) * mm, "end": v(4.24, 26.74) * mm});
            skLineSegment(sketch, "E58.29.5", {"start": v(4.47, 26.69) * mm, "end": v(4.24, 26.74) * mm});
            skArc(sketch, "E58.29.6", {"start": v(4.83, 26.4) * mm, "mid": v(4.68, 26.59) * mm, "end": v(4.47, 26.69) * mm});
            skArc(sketch, "E58.29.7", {"start": v(5.28, 24.84) * mm, "mid": v(5.1, 25.64) * mm, "end": v(4.83, 26.4) * mm});
            skLineSegment(sketch, "E58.29.8", {"start": v(5.28, 24.84) * mm, "end": v(5.02, 23.6) * mm});
            skArc(sketch, "E58.29.9", {"start": v(5.02, 23.6) * mm, "mid": v(5.08, 23.22) * mm, "end": v(5.4, 23) * mm});
            skArc(sketch, "E59.trimOffspring", {"start": v(-7.77, 22.3) * mm, "mid": v(-8.47, 22.05) * mm, "end": v(-9.15, 21.78) * mm});
            skArc(sketch, "E60.trimOffspring", {"start": v(1.97, 23.54) * mm, "mid": v(1.24, 23.59) * mm, "end": v(0.5, 23.62) * mm});
            skArc(sketch, "E61.trimOffspring", {"start": v(6.83, 22.61) * mm, "mid": v(6.11, 22.82) * mm, "end": v(5.4, 23) * mm});
            skArc(sketch, "E62.trimOffspring", {"start": v(11.38, 20.7) * mm, "mid": v(10.72, 21.05) * mm, "end": v(10.06, 21.37) * mm});
            skArc(sketch, "E63.trimOffspring", {"start": v(15.43, 17.88) * mm, "mid": v(14.87, 18.36) * mm, "end": v(14.28, 18.81) * mm});
            skArc(sketch, "E64.trimOffspring", {"start": v(18.81, 14.28) * mm, "mid": v(18.36, 14.87) * mm, "end": v(17.88, 15.43) * mm});
            skArc(sketch, "E65.trimOffspring", {"start": v(21.37, 10.06) * mm, "mid": v(21.05, 10.72) * mm, "end": v(20.7, 11.38) * mm});
            skArc(sketch, "E66.trimOffspring", {"start": v(-12.24, 20.2) * mm, "mid": v(-12.87, 19.81) * mm, "end": v(-13.48, 19.4) * mm});
            skArc(sketch, "E67.trimOffspring", {"start": v(-16.17, 17.22) * mm, "mid": v(-16.7, 16.7) * mm, "end": v(-17.22, 16.17) * mm});
            skArc(sketch, "E68.trimOffspring", {"start": v(-19.4, 13.48) * mm, "mid": v(-19.81, 12.87) * mm, "end": v(-20.2, 12.24) * mm});
            skArc(sketch, "E69.trimOffspring", {"start": v(-21.78, 9.15) * mm, "mid": v(-22.05, 8.47) * mm, "end": v(-22.3, 7.77) * mm});
            skArc(sketch, "E70.trimOffspring", {"start": v(-23.2, 4.42) * mm, "mid": v(-23.33, 3.7) * mm, "end": v(-23.44, 2.96) * mm});
            skArc(sketch, "E71.trimOffspring", {"start": v(23, 5.4) * mm, "mid": v(22.82, 6.11) * mm, "end": v(22.61, 6.83) * mm});
            skArc(sketch, "E72.trimOffspring", {"start": v(23.62, 0.5) * mm, "mid": v(23.59, 1.24) * mm, "end": v(23.54, 1.97) * mm});
            skArc(sketch, "E73.trimOffspring", {"start": v(-23.62, -0.5) * mm, "mid": v(-23.59, -1.24) * mm, "end": v(-23.54, -1.97) * mm});
            skArc(sketch, "E74.trimOffspring", {"start": v(-23, -5.4) * mm, "mid": v(-22.82, -6.11) * mm, "end": v(-22.61, -6.83) * mm});
            skArc(sketch, "E75.trimOffspring", {"start": v(-21.37, -10.06) * mm, "mid": v(-21.05, -10.72) * mm, "end": v(-20.7, -11.38) * mm});
            skArc(sketch, "E76.trimOffspring", {"start": v(-18.81, -14.28) * mm, "mid": v(-18.36, -14.87) * mm, "end": v(-17.88, -15.43) * mm});
            skArc(sketch, "E77.trimOffspring", {"start": v(-15.43, -17.88) * mm, "mid": v(-14.87, -18.36) * mm, "end": v(-14.28, -18.81) * mm});
            skArc(sketch, "E78.trimOffspring", {"start": v(-11.38, -20.7) * mm, "mid": v(-10.72, -21.05) * mm, "end": v(-10.06, -21.37) * mm});
            skArc(sketch, "E79.trimOffspring", {"start": v(-6.83, -22.61) * mm, "mid": v(-6.11, -22.82) * mm, "end": v(-5.4, -23) * mm});
            skArc(sketch, "E80.trimOffspring", {"start": v(-1.97, -23.54) * mm, "mid": v(-1.24, -23.59) * mm, "end": v(-0.5, -23.62) * mm});
            skArc(sketch, "E81.trimOffspring", {"start": v(2.96, -23.44) * mm, "mid": v(3.7, -23.33) * mm, "end": v(4.42, -23.2) * mm});
            skArc(sketch, "E82.trimOffspring", {"start": v(7.77, -22.3) * mm, "mid": v(8.47, -22.05) * mm, "end": v(9.15, -21.78) * mm});
            skArc(sketch, "E83.trimOffspring", {"start": v(12.24, -20.2) * mm, "mid": v(12.87, -19.81) * mm, "end": v(13.48, -19.4) * mm});
            skArc(sketch, "E84.trimOffspring", {"start": v(16.17, -17.22) * mm, "mid": v(16.7, -16.7) * mm, "end": v(17.22, -16.17) * mm});
            skArc(sketch, "E85.trimOffspring", {"start": v(19.4, -13.48) * mm, "mid": v(19.81, -12.87) * mm, "end": v(20.2, -12.24) * mm});
            skArc(sketch, "E86.trimOffspring", {"start": v(21.78, -9.15) * mm, "mid": v(22.05, -8.47) * mm, "end": v(22.3, -7.77) * mm});
            skArc(sketch, "E87.trimOffspring", {"start": v(23.2, -4.42) * mm, "mid": v(23.33, -3.7) * mm, "end": v(23.44, -2.96) * mm});
            skSolve(sketch);
        }
        {
            var Q0;
            Q0=makeQuery(id+"F0.imprint","IMPRINT",FACE,{"disambiguationData":[TD([[makeQuery(id+"F0.imprint","IMPRINT",EDGE,{"derivedFrom":sQuery(id+"F0.wireOp",EDGE,"E0")}),1.0]])]});
            var Q1;
            Q1=makeQuery(id+"F2.imprint","IMPRINT",FACE,{"disambiguationData":[TD([[makeQuery(id+"F2.imprint","IMPRINT",EDGE,{"derivedFrom":sQuery(id+"F2.wireOp",EDGE,"E44")}),1.0]])]});
            var Q2;
            Q2=sQuery(id+"F0.wireOp",VERTEX,"E5.MirrorCS.start");
            var Q3;
            Q3=sQuery(id+"F2.wireOp",VERTEX,"E58.2.4.start");
            loft(context, id + "F3", {"sheetProfilesArray" : [{ "sheetProfileEntities" : qUnion([Q0]) }, { "sheetProfileEntities" : qUnion([Q1]) }], "matchConnections" : true, "connections" : [{ "connectionEntities" : qUnion([Q2, Q3]), "connectionEdgeQueries" : qUnion([]), "connectionEdgeParameters" : [] }]});
        }
        {
            var Q0;
            Q0=makeQuery(id+"F3.opLoft","CAP_FACE",FACE,{"disambiguationData":[OSD([makeQuery(id+"F2.imprint","IMPRINT",FACE,{"disambiguationData":[TD([[makeQuery(id+"F2.imprint","IMPRINT",EDGE,{"derivedFrom":sQuery(id+"F2.wireOp",EDGE,"E44")}),1.0]])]})])],"isStart":true});
            var sketch = newSketch(context, id + "F4", { "sketchPlane" : qUnion([Q0])});
            skCircle(sketch, "E88", {"center": v(0, 0) * mm, "radius": 6.35 * mm});
            skSolve(sketch);
        }
        {
            var Q0;
            Q0 = qSketchRegion(id + "F4", true);
            extrude(context, id + "F5", {"entities" : qUnion([Q0]), "operationType" : NewBodyOperationType.REMOVE, "endBound" : BoundingType.THROUGH_ALL, "oppositeDirection" : true, "depth" : 25.4 * mm});
        }
    });
